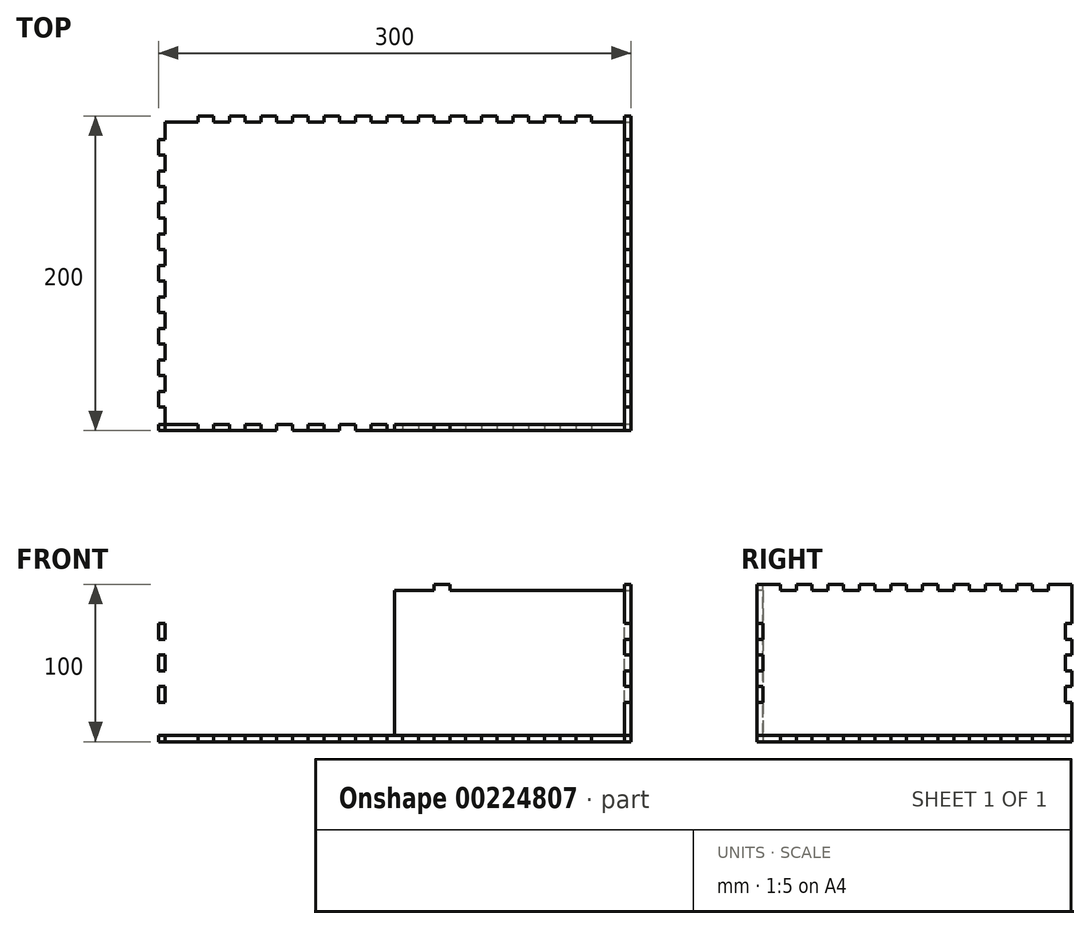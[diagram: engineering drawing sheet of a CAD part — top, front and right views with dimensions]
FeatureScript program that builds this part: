
annotation { "Feature Type Name" : "Feature", "Feature Type Description" : "" }
export const myFeature = defineFeature(function(context is Context, id is Id, definition is map)
    precondition{}
    {
        {
            var Q0;
            Q0=qCreatedBy(makeId("Top.planeOp"),FACE);
            var sketch = newSketch(context, id + "F0", { "sketchPlane" : qUnion([Q0])});
            skLineSegment(sketch, "E0.left", {"start": v(150, -85) * mm, "end": v(150, -75) * mm});
            skLineSegment(sketch, "E0.right", {"start": v(-150, -85) * mm, "end": v(-150, -75) * mm});
            skPoint(sketch, "E0.middle", {"position": v(0, 0) * mm});
            skLineSegment(sketch, "E1", {"start": v(0, 100) * mm, "end": v(0, 96) * mm});
            skPoint(sketch, "E1.endSnap0", {"position": v(0, 100) * mm});
            skLineSegment(sketch, "E2", {"start": v(0, 96) * mm, "end": v(5, 96) * mm});
            skLineSegment(sketch, "E3", {"start": v(5, 96) * mm, "end": v(5, 100) * mm});
            skLineSegment(sketch, "E4.MirrorCS", {"start": v(-5, 96) * mm, "end": v(-5, 100) * mm});
            skLineSegment(sketch, "E5.1.0.0", {"start": v(20, 96) * mm, "end": v(25, 96) * mm});
            skPoint(sketch, "E5.1.0.1", {"position": v(20, 100) * mm});
            skLineSegment(sketch, "E5.1.0.2", {"start": v(25, 96) * mm, "end": v(25, 100) * mm});
            skLineSegment(sketch, "E5.1.0.3", {"start": v(15, 96) * mm, "end": v(15, 100) * mm});
            skLineSegment(sketch, "E5.2.0.0", {"start": v(40, 96) * mm, "end": v(45, 96) * mm});
            skPoint(sketch, "E5.2.0.1", {"position": v(40, 100) * mm});
            skLineSegment(sketch, "E5.2.0.2", {"start": v(45, 96) * mm, "end": v(45, 100) * mm});
            skLineSegment(sketch, "E5.2.0.3", {"start": v(35, 96) * mm, "end": v(35, 100) * mm});
            skLineSegment(sketch, "E5.3.0.0", {"start": v(60, 96) * mm, "end": v(65, 96) * mm});
            skPoint(sketch, "E5.3.0.1", {"position": v(60, 100) * mm});
            skLineSegment(sketch, "E5.3.0.2", {"start": v(65, 96) * mm, "end": v(65, 100) * mm});
            skLineSegment(sketch, "E5.3.0.3", {"start": v(55, 96) * mm, "end": v(55, 100) * mm});
            skLineSegment(sketch, "E5.4.0.0", {"start": v(80, 96) * mm, "end": v(85, 96) * mm});
            skPoint(sketch, "E5.4.0.1", {"position": v(80, 100) * mm});
            skLineSegment(sketch, "E5.4.0.2", {"start": v(85, 96) * mm, "end": v(85, 100) * mm});
            skLineSegment(sketch, "E5.4.0.3", {"start": v(75, 96) * mm, "end": v(75, 100) * mm});
            skLineSegment(sketch, "E5.5.0.0", {"start": v(100, 96) * mm, "end": v(105, 96) * mm});
            skPoint(sketch, "E5.5.0.1", {"position": v(100, 100) * mm});
            skLineSegment(sketch, "E5.5.0.2", {"start": v(105, 96) * mm, "end": v(105, 100) * mm});
            skLineSegment(sketch, "E5.5.0.3", {"start": v(95, 96) * mm, "end": v(95, 100) * mm});
            skLineSegment(sketch, "E5.direction1", {"start": v(-5, 96) * mm, "end": v(15, 96) * mm, "construction": true});
            skLineSegment(sketch, "E6", {"start": v(0, 96) * mm, "end": v(146, 96) * mm});
            skLineSegment(sketch, "E7", {"start": v(-146, 96) * mm, "end": v(146, 96) * mm});
            skLineSegment(sketch, "E8.trimOffspring", {"start": v(5, 100) * mm, "end": v(-5, 100) * mm});
            skLineSegment(sketch, "E9.trimOffspring", {"start": v(25, 100) * mm, "end": v(15, 100) * mm});
            skLineSegment(sketch, "E10.trimOffspring", {"start": v(45, 100) * mm, "end": v(35, 100) * mm});
            skLineSegment(sketch, "E11.trimOffspring", {"start": v(65, 100) * mm, "end": v(55, 100) * mm});
            skLineSegment(sketch, "E12.trimOffspring", {"start": v(85, 100) * mm, "end": v(75, 100) * mm});
            skLineSegment(sketch, "E13.trimOffspring", {"start": v(105, 100) * mm, "end": v(95, 100) * mm});
            skLineSegment(sketch, "E14.trimOffspring", {"start": v(125, 100) * mm, "end": v(115, 100) * mm});
            skLineSegment(sketch, "E15.MirrorCS", {"start": v(-65, 96) * mm, "end": v(-65, 100) * mm});
            skLineSegment(sketch, "E16.MirrorCS", {"start": v(-125, 96) * mm, "end": v(-125, 100) * mm});
            skLineSegment(sketch, "E17.MirrorCS", {"start": v(-105, 96) * mm, "end": v(-105, 100) * mm});
            skLineSegment(sketch, "E18.MirrorCS", {"start": v(-85, 96) * mm, "end": v(-85, 100) * mm});
            skLineSegment(sketch, "E19.MirrorCS", {"start": v(-45, 96) * mm, "end": v(-45, 100) * mm});
            skLineSegment(sketch, "E20.MirrorCS", {"start": v(-15, 96) * mm, "end": v(-15, 100) * mm});
            skLineSegment(sketch, "E21.MirrorCS", {"start": v(-25, 96) * mm, "end": v(-25, 100) * mm});
            skLineSegment(sketch, "E22.MirrorCS", {"start": v(-75, 96) * mm, "end": v(-75, 100) * mm});
            skLineSegment(sketch, "E23.MirrorCS", {"start": v(-65, 100) * mm, "end": v(-55, 100) * mm});
            skLineSegment(sketch, "E24.MirrorCS", {"start": v(-60, 96) * mm, "end": v(-65, 96) * mm});
            skLineSegment(sketch, "E25.MirrorCS", {"start": v(-125, 100) * mm, "end": v(-115, 100) * mm});
            skLineSegment(sketch, "E26.MirrorCS", {"start": v(-95, 96) * mm, "end": v(-95, 100) * mm});
            skLineSegment(sketch, "E27.MirrorCS", {"start": v(-20, 96) * mm, "end": v(-25, 96) * mm});
            skLineSegment(sketch, "E28.MirrorCS", {"start": v(-55, 96) * mm, "end": v(-55, 100) * mm});
            skLineSegment(sketch, "E29.MirrorCS", {"start": v(-105, 100) * mm, "end": v(-95, 100) * mm});
            skLineSegment(sketch, "E30.MirrorCS", {"start": v(-45, 100) * mm, "end": v(-35, 100) * mm});
            skLineSegment(sketch, "E31.MirrorCS", {"start": v(-40, 96) * mm, "end": v(-45, 96) * mm});
            skLineSegment(sketch, "E32.MirrorCS", {"start": v(-35, 96) * mm, "end": v(-35, 100) * mm});
            skLineSegment(sketch, "E33.MirrorCS", {"start": v(-85, 100) * mm, "end": v(-75, 100) * mm});
            skLineSegment(sketch, "E34.MirrorCS", {"start": v(-25, 100) * mm, "end": v(-15, 100) * mm});
            skLineSegment(sketch, "E35.MirrorCS", {"start": v(-100, 96) * mm, "end": v(-105, 96) * mm});
            skLineSegment(sketch, "E36.MirrorCS", {"start": v(-115, 96) * mm, "end": v(-115, 100) * mm});
            skLineSegment(sketch, "E37.MirrorCS", {"start": v(-80, 96) * mm, "end": v(-85, 96) * mm});
            skLineSegment(sketch, "E38.MirrorCS", {"start": v(-120, 96) * mm, "end": v(-125, 96) * mm});
            skPoint(sketch, "E39.MirrorP", {"position": v(-80, 100) * mm});
            skPoint(sketch, "E40.MirrorP", {"position": v(-60, 100) * mm});
            skPoint(sketch, "E41.MirrorP", {"position": v(-100, 100) * mm});
            skPoint(sketch, "E42.MirrorP", {"position": v(-120, 100) * mm});
            skPoint(sketch, "E43.MirrorP", {"position": v(-20, 100) * mm});
            skPoint(sketch, "E44.MirrorP", {"position": v(-40, 100) * mm});
            skLineSegment(sketch, "E45.trimOffspring", {"start": v(-15, 100) * mm, "end": v(-25, 100) * mm});
            skLineSegment(sketch, "E46.trimOffspring", {"start": v(-35, 100) * mm, "end": v(-45, 100) * mm});
            skLineSegment(sketch, "E47.trimOffspring", {"start": v(-55, 100) * mm, "end": v(-65, 100) * mm});
            skLineSegment(sketch, "E48.trimOffspring", {"start": v(-75, 100) * mm, "end": v(-85, 100) * mm});
            skLineSegment(sketch, "E49.trimOffspring", {"start": v(-95, 100) * mm, "end": v(-105, 100) * mm});
            skLineSegment(sketch, "E50.trimOffspring", {"start": v(-115, 100) * mm, "end": v(-120, 100) * mm});
            skLineSegment(sketch, "E51.MirrorCS", {"start": v(-105, -96) * mm, "end": v(-105, -100) * mm});
            skLineSegment(sketch, "E52.MirrorCS", {"start": v(-115, -96) * mm, "end": v(-115, -100) * mm});
            skLineSegment(sketch, "E53.MirrorCS", {"start": v(-65, -96) * mm, "end": v(-65, -100) * mm});
            skLineSegment(sketch, "E54.MirrorCS", {"start": v(-55, -96) * mm, "end": v(-55, -100) * mm});
            skLineSegment(sketch, "E55.MirrorCS", {"start": v(-75, -96) * mm, "end": v(-75, -100) * mm});
            skLineSegment(sketch, "E56.MirrorCS", {"start": v(-25, -96) * mm, "end": v(-25, -100) * mm});
            skLineSegment(sketch, "E57.MirrorCS", {"start": v(-15, -96) * mm, "end": v(-15, -100) * mm});
            skLineSegment(sketch, "E58.MirrorCS", {"start": v(-45, -96) * mm, "end": v(-45, -100) * mm});
            skLineSegment(sketch, "E59.MirrorCS", {"start": v(-35, -96) * mm, "end": v(-35, -100) * mm});
            skLineSegment(sketch, "E60.MirrorCS", {"start": v(-95, -96) * mm, "end": v(-95, -100) * mm});
            skLineSegment(sketch, "E61.MirrorCS", {"start": v(-85, -96) * mm, "end": v(-85, -100) * mm});
            skLineSegment(sketch, "E62.MirrorCS", {"start": v(-125, -100) * mm, "end": v(-115, -100) * mm});
            skLineSegment(sketch, "E63.MirrorCS", {"start": v(-120, -96) * mm, "end": v(-125, -96) * mm});
            skLineSegment(sketch, "E64.MirrorCS", {"start": v(85, -96) * mm, "end": v(85, -100) * mm});
            skLineSegment(sketch, "E65.MirrorCS", {"start": v(125, -96) * mm, "end": v(125, -100) * mm});
            skLineSegment(sketch, "E66.MirrorCS", {"start": v(-115, -100) * mm, "end": v(-120, -100) * mm});
            skLineSegment(sketch, "E67.MirrorCS", {"start": v(-125, -96) * mm, "end": v(-125, -100) * mm});
            skLineSegment(sketch, "E68.MirrorCS", {"start": v(5, -100) * mm, "end": v(-5, -100) * mm});
            skLineSegment(sketch, "E69.MirrorCS", {"start": v(55, -96) * mm, "end": v(55, -100) * mm});
            skLineSegment(sketch, "E70.MirrorCS", {"start": v(-95, -100) * mm, "end": v(-105, -100) * mm});
            skLineSegment(sketch, "E71.MirrorCS", {"start": v(45, -96) * mm, "end": v(45, -100) * mm});
            skLineSegment(sketch, "E72.MirrorCS", {"start": v(15, -96) * mm, "end": v(15, -100) * mm});
            skLineSegment(sketch, "E73.MirrorCS", {"start": v(25, -96) * mm, "end": v(25, -100) * mm});
            skLineSegment(sketch, "E74.MirrorCS", {"start": v(-5, -96) * mm, "end": v(-5, -100) * mm});
            skLineSegment(sketch, "E75.MirrorCS", {"start": v(5, -96) * mm, "end": v(5, -100) * mm});
            skLineSegment(sketch, "E76.MirrorCS", {"start": v(0, -96) * mm, "end": v(5, -96) * mm});
            skLineSegment(sketch, "E77.MirrorCS", {"start": v(0, -100) * mm, "end": v(0, -96) * mm});
            skLineSegment(sketch, "E78.MirrorCS", {"start": v(65, -96) * mm, "end": v(65, -100) * mm});
            skLineSegment(sketch, "E79.MirrorCS", {"start": v(35, -96) * mm, "end": v(35, -100) * mm});
            skLineSegment(sketch, "E80.MirrorCS", {"start": v(95, -96) * mm, "end": v(95, -100) * mm});
            skLineSegment(sketch, "E81.MirrorCS", {"start": v(-55, -100) * mm, "end": v(-65, -100) * mm});
            skLineSegment(sketch, "E82.MirrorCS", {"start": v(105, -96) * mm, "end": v(105, -100) * mm});
            skLineSegment(sketch, "E83.MirrorCS", {"start": v(-35, -100) * mm, "end": v(-45, -100) * mm});
            skLineSegment(sketch, "E84.MirrorCS", {"start": v(-85, -100) * mm, "end": v(-75, -100) * mm});
            skLineSegment(sketch, "E85.MirrorCS", {"start": v(-15, -100) * mm, "end": v(-25, -100) * mm});
            skLineSegment(sketch, "E86.MirrorCS", {"start": v(75, -96) * mm, "end": v(75, -100) * mm});
            skLineSegment(sketch, "E87.MirrorCS", {"start": v(115, -96) * mm, "end": v(115, -100) * mm});
            skLineSegment(sketch, "E88.MirrorCS", {"start": v(45, -100) * mm, "end": v(35, -100) * mm});
            skLineSegment(sketch, "E89.MirrorCS", {"start": v(-45, -100) * mm, "end": v(-35, -100) * mm});
            skLineSegment(sketch, "E90.MirrorCS", {"start": v(25, -100) * mm, "end": v(15, -100) * mm});
            skLineSegment(sketch, "E91.MirrorCS", {"start": v(-60, -96) * mm, "end": v(-65, -96) * mm});
            skLineSegment(sketch, "E92.MirrorCS", {"start": v(-80, -96) * mm, "end": v(-85, -96) * mm});
            skLineSegment(sketch, "E93.MirrorCS", {"start": v(80, -96) * mm, "end": v(85, -96) * mm});
            skLineSegment(sketch, "E94.MirrorCS", {"start": v(120, -96) * mm, "end": v(125, -96) * mm});
            skLineSegment(sketch, "E95.MirrorCS", {"start": v(-105, -100) * mm, "end": v(-95, -100) * mm});
            skLineSegment(sketch, "E96.MirrorCS", {"start": v(-65, -100) * mm, "end": v(-55, -100) * mm});
            skLineSegment(sketch, "E97.MirrorCS", {"start": v(40, -96) * mm, "end": v(45, -96) * mm});
            skLineSegment(sketch, "E98.MirrorCS", {"start": v(20, -96) * mm, "end": v(25, -96) * mm});
            skLineSegment(sketch, "E99.MirrorCS", {"start": v(60, -96) * mm, "end": v(65, -96) * mm});
            skLineSegment(sketch, "E100.MirrorCS", {"start": v(125, -100) * mm, "end": v(115, -100) * mm});
            skLineSegment(sketch, "E101.MirrorCS", {"start": v(-75, -100) * mm, "end": v(-85, -100) * mm});
            skLineSegment(sketch, "E102.MirrorCS", {"start": v(-100, -96) * mm, "end": v(-105, -96) * mm});
            skLineSegment(sketch, "E103.MirrorCS", {"start": v(105, -100) * mm, "end": v(95, -100) * mm});
            skLineSegment(sketch, "E104.MirrorCS", {"start": v(-20, -96) * mm, "end": v(-25, -96) * mm});
            skLineSegment(sketch, "E105.MirrorCS", {"start": v(-25, -100) * mm, "end": v(-15, -100) * mm});
            skLineSegment(sketch, "E106.MirrorCS", {"start": v(85, -100) * mm, "end": v(75, -100) * mm});
            skLineSegment(sketch, "E107.MirrorCS", {"start": v(100, -96) * mm, "end": v(105, -96) * mm});
            skLineSegment(sketch, "E108.MirrorCS", {"start": v(140, -96) * mm, "end": v(145, -96) * mm});
            skLineSegment(sketch, "E109.MirrorCS", {"start": v(65, -100) * mm, "end": v(55, -100) * mm});
            skLineSegment(sketch, "E110.MirrorCS", {"start": v(-40, -96) * mm, "end": v(-45, -96) * mm});
            skPoint(sketch, "E111.MirrorP", {"position": v(80, -100) * mm});
            skPoint(sketch, "E112.MirrorP", {"position": v(-20, -100) * mm});
            skPoint(sketch, "E113.MirrorP", {"position": v(60, -100) * mm});
            skPoint(sketch, "E114.MirrorP", {"position": v(-120, -100) * mm});
            skPoint(sketch, "E115.MirrorP", {"position": v(-100, -100) * mm});
            skLineSegment(sketch, "E116.MirrorCS", {"start": v(-5, -96) * mm, "end": v(15, -96) * mm, "construction": true});
            skPoint(sketch, "E117.MirrorP", {"position": v(40, -100) * mm});
            skPoint(sketch, "E118.MirrorP", {"position": v(20, -100) * mm});
            skPoint(sketch, "E119.MirrorP", {"position": v(0, -100) * mm});
            skPoint(sketch, "E120.MirrorP", {"position": v(-60, -100) * mm});
            skPoint(sketch, "E121.MirrorP", {"position": v(120, -100) * mm});
            skPoint(sketch, "E122.MirrorP", {"position": v(-80, -100) * mm});
            skPoint(sketch, "E123.MirrorP", {"position": v(100, -100) * mm});
            skPoint(sketch, "E124.MirrorP", {"position": v(-40, -100) * mm});
            skLineSegment(sketch, "E125", {"start": v(-146, -96) * mm, "end": v(146, -96) * mm});
            skPoint(sketch, "E126.orphan", {"position": v(-150, -100) * mm});
            skLineSegment(sketch, "E127.trimOffspring", {"start": v(-115, -100) * mm, "end": v(-125, -100) * mm});
            skLineSegment(sketch, "E128", {"start": v(150, 0) * mm, "end": v(146, 0) * mm});
            skPoint(sketch, "E128.endSnap0", {"position": v(150, 0) * mm});
            skLineSegment(sketch, "E129", {"start": v(150, -5) * mm, "end": v(146, -5) * mm});
            skLineSegment(sketch, "E130.MirrorCS", {"start": v(150, 5) * mm, "end": v(146, 5) * mm});
            skLineSegment(sketch, "E131", {"start": v(146, 5) * mm, "end": v(146, -96) * mm});
            skLineSegment(sketch, "E132", {"start": v(146, -96) * mm, "end": v(146, 96) * mm});
            skPoint(sketch, "E133.0.1.0", {"position": v(150, -20) * mm});
            skLineSegment(sketch, "E133.0.1.1", {"start": v(150, -25) * mm, "end": v(146, -25) * mm});
            skLineSegment(sketch, "E133.0.1.3", {"start": v(150, -15) * mm, "end": v(146, -15) * mm});
            skPoint(sketch, "E133.0.2.0", {"position": v(150, -40) * mm});
            skLineSegment(sketch, "E133.0.2.1", {"start": v(150, -45) * mm, "end": v(146, -45) * mm});
            skLineSegment(sketch, "E133.0.2.3", {"start": v(150, -35) * mm, "end": v(146, -35) * mm});
            skPoint(sketch, "E133.0.3.0", {"position": v(150, -60) * mm});
            skLineSegment(sketch, "E133.0.3.1", {"start": v(150, -65) * mm, "end": v(146, -65) * mm});
            skLineSegment(sketch, "E133.0.3.3", {"start": v(150, -55) * mm, "end": v(146, -55) * mm});
            skPoint(sketch, "E133.0.4.0", {"position": v(150, -80) * mm});
            skLineSegment(sketch, "E133.0.4.1", {"start": v(150, -85) * mm, "end": v(146, -85) * mm});
            skLineSegment(sketch, "E133.0.4.2", {"start": v(150, -80) * mm, "end": v(146, -80) * mm});
            skLineSegment(sketch, "E133.0.4.3", {"start": v(150, -75) * mm, "end": v(146, -75) * mm});
            skLineSegment(sketch, "E133.direction1", {"start": v(146, -5) * mm, "end": v(171, -5) * mm, "construction": true});
            skLineSegment(sketch, "E133.direction2", {"start": v(146, -5) * mm, "end": v(146, -25) * mm, "construction": true});
            skLineSegment(sketch, "E134.trimOffspring", {"start": v(150, -5) * mm, "end": v(150, 5) * mm});
            skLineSegment(sketch, "E135.trimOffspring", {"start": v(150, -25) * mm, "end": v(150, -15) * mm});
            skLineSegment(sketch, "E136.trimOffspring", {"start": v(150, -45) * mm, "end": v(150, -35) * mm});
            skLineSegment(sketch, "E137.trimOffspring", {"start": v(150, -65) * mm, "end": v(150, -55) * mm});
            skLineSegment(sketch, "E138.MirrorCS", {"start": v(150, 25) * mm, "end": v(146, 25) * mm});
            skLineSegment(sketch, "E139.MirrorCS", {"start": v(150, 65) * mm, "end": v(150, 55) * mm});
            skLineSegment(sketch, "E140.MirrorCS", {"start": v(150, 45) * mm, "end": v(150, 35) * mm});
            skLineSegment(sketch, "E141.MirrorCS", {"start": v(150, 55) * mm, "end": v(146, 55) * mm});
            skLineSegment(sketch, "E142.MirrorCS", {"start": v(150, 35) * mm, "end": v(146, 35) * mm});
            skLineSegment(sketch, "E143.MirrorCS", {"start": v(150, 45) * mm, "end": v(146, 45) * mm});
            skLineSegment(sketch, "E144.MirrorCS", {"start": v(150, 75) * mm, "end": v(146, 75) * mm});
            skLineSegment(sketch, "E145.MirrorCS", {"start": v(150, 65) * mm, "end": v(146, 65) * mm});
            skLineSegment(sketch, "E146.MirrorCS", {"start": v(150, 15) * mm, "end": v(146, 15) * mm});
            skLineSegment(sketch, "E147.MirrorCS", {"start": v(150, 85) * mm, "end": v(146, 85) * mm});
            skPoint(sketch, "E148.MirrorP", {"position": v(150, 60) * mm});
            skPoint(sketch, "E149.MirrorP", {"position": v(150, 40) * mm});
            skLineSegment(sketch, "E150.MirrorCS", {"start": v(150, 25) * mm, "end": v(150, 15) * mm});
            skLineSegment(sketch, "E151.MirrorCS", {"start": v(150, 85) * mm, "end": v(150, 75) * mm});
            skPoint(sketch, "E152.MirrorP", {"position": v(150, 80) * mm});
            skPoint(sketch, "E153.MirrorP", {"position": v(150, 20) * mm});
            skLineSegment(sketch, "E154.trimOffspring", {"start": v(150, 75) * mm, "end": v(150, 85) * mm});
            skLineSegment(sketch, "E155.trimOffspring", {"start": v(150, 55) * mm, "end": v(150, 65) * mm});
            skLineSegment(sketch, "E156.trimOffspring", {"start": v(150, 35) * mm, "end": v(150, 45) * mm});
            skLineSegment(sketch, "E157.trimOffspring", {"start": v(150, 15) * mm, "end": v(150, 25) * mm});
            skPoint(sketch, "E158.MirrorCS.end.orphan", {"position": v(146, 20) * mm});
            skPoint(sketch, "E159.MirrorCS.end.orphan", {"position": v(146, 40) * mm});
            skPoint(sketch, "E160.MirrorCS.end.orphan", {"position": v(146, 60) * mm});
            skPoint(sketch, "E161.MirrorCS.end.orphan", {"position": v(146, 80) * mm});
            skPoint(sketch, "E133.0.3.2.end.orphan", {"position": v(146, -60) * mm});
            skPoint(sketch, "E133.0.3.2.start.orphan", {"position": v(150, -60) * mm});
            skPoint(sketch, "E133.0.2.2.end.orphan", {"position": v(146, -40) * mm});
            skPoint(sketch, "E133.0.2.2.start.orphan", {"position": v(150, -40) * mm});
            skPoint(sketch, "E133.0.1.2.end.orphan", {"position": v(146, -20) * mm});
            skPoint(sketch, "E133.0.1.2.start.orphan", {"position": v(150, -20) * mm});
            skLineSegment(sketch, "E162.MirrorCS", {"start": v(-150, 45) * mm, "end": v(-150, 35) * mm});
            skLineSegment(sketch, "E163.MirrorCS", {"start": v(-150, 85) * mm, "end": v(-150, 75) * mm});
            skLineSegment(sketch, "E164.MirrorCS", {"start": v(-150, 25) * mm, "end": v(-150, 15) * mm});
            skLineSegment(sketch, "E165.MirrorCS", {"start": v(-150, 65) * mm, "end": v(-150, 55) * mm});
            skLineSegment(sketch, "E166.MirrorCS", {"start": v(-150, 45) * mm, "end": v(-146, 45) * mm});
            skLineSegment(sketch, "E167.MirrorCS", {"start": v(-150, 75) * mm, "end": v(-146, 75) * mm});
            skLineSegment(sketch, "E168.MirrorCS", {"start": v(-150, -80) * mm, "end": v(-146, -80) * mm});
            skLineSegment(sketch, "E169.MirrorCS", {"start": v(-150, 85) * mm, "end": v(-146, 85) * mm});
            skLineSegment(sketch, "E170.MirrorCS", {"start": v(-150, 75) * mm, "end": v(-150, 85) * mm});
            skLineSegment(sketch, "E171.MirrorCS", {"start": v(-150, 0) * mm, "end": v(-146, 0) * mm});
            skLineSegment(sketch, "E172.MirrorCS", {"start": v(-150, 35) * mm, "end": v(-150, 45) * mm});
            skLineSegment(sketch, "E173.MirrorCS", {"start": v(-150, 35) * mm, "end": v(-146, 35) * mm});
            skLineSegment(sketch, "E174.MirrorCS", {"start": v(-150, 55) * mm, "end": v(-146, 55) * mm});
            skLineSegment(sketch, "E175.MirrorCS", {"start": v(-150, -5) * mm, "end": v(-146, -5) * mm});
            skLineSegment(sketch, "E176.MirrorCS", {"start": v(-150, 55) * mm, "end": v(-150, 65) * mm});
            skLineSegment(sketch, "E177.MirrorCS", {"start": v(-150, 15) * mm, "end": v(-150, 25) * mm});
            skLineSegment(sketch, "E178.MirrorCS", {"start": v(-150, 65) * mm, "end": v(-146, 65) * mm});
            skLineSegment(sketch, "E179.MirrorCS", {"start": v(-150, 25) * mm, "end": v(-146, 25) * mm});
            skLineSegment(sketch, "E180.MirrorCS", {"start": v(-150, 15) * mm, "end": v(-146, 15) * mm});
            skLineSegment(sketch, "E181.MirrorCS", {"start": v(-150, -15) * mm, "end": v(-146, -15) * mm});
            skLineSegment(sketch, "E182.MirrorCS", {"start": v(-150, -35) * mm, "end": v(-146, -35) * mm});
            skLineSegment(sketch, "E183.MirrorCS", {"start": v(-150, -65) * mm, "end": v(-146, -65) * mm});
            skLineSegment(sketch, "E184.MirrorCS", {"start": v(-150, -55) * mm, "end": v(-146, -55) * mm});
            skLineSegment(sketch, "E185.MirrorCS", {"start": v(-146, -5) * mm, "end": v(-146, -25) * mm, "construction": true});
            skLineSegment(sketch, "E186.MirrorCS", {"start": v(-150, -5) * mm, "end": v(-150, 5) * mm});
            skLineSegment(sketch, "E187.MirrorCS", {"start": v(-150, 5) * mm, "end": v(-146, 5) * mm});
            skLineSegment(sketch, "E188.MirrorCS", {"start": v(-150, -45) * mm, "end": v(-150, -35) * mm});
            skLineSegment(sketch, "E189.MirrorCS", {"start": v(-150, -75) * mm, "end": v(-146, -75) * mm});
            skLineSegment(sketch, "E190.MirrorCS", {"start": v(-150, -25) * mm, "end": v(-150, -15) * mm});
            skLineSegment(sketch, "E191.MirrorCS", {"start": v(-150, -45) * mm, "end": v(-146, -45) * mm});
            skLineSegment(sketch, "E192.MirrorCS", {"start": v(-150, -85) * mm, "end": v(-146, -85) * mm});
            skLineSegment(sketch, "E193.MirrorCS", {"start": v(-150, -65) * mm, "end": v(-150, -55) * mm});
            skLineSegment(sketch, "E194.MirrorCS", {"start": v(-150, -25) * mm, "end": v(-146, -25) * mm});
            skPoint(sketch, "E195.MirrorP", {"position": v(-150, -20) * mm});
            skPoint(sketch, "E196.MirrorP", {"position": v(-150, 80) * mm});
            skPoint(sketch, "E197.MirrorP", {"position": v(-150, -40) * mm});
            skPoint(sketch, "E198.MirrorP", {"position": v(-150, 40) * mm});
            skPoint(sketch, "E199.MirrorP", {"position": v(-150, 60) * mm});
            skPoint(sketch, "E200.MirrorP", {"position": v(-150, 20) * mm});
            skPoint(sketch, "E201.MirrorP", {"position": v(-150, -60) * mm});
            skPoint(sketch, "E202.MirrorP", {"position": v(-146, 80) * mm});
            skPoint(sketch, "E203.MirrorP", {"position": v(-150, -80) * mm});
            skPoint(sketch, "E204.MirrorP", {"position": v(-146, -40) * mm});
            skPoint(sketch, "E205.MirrorP", {"position": v(-150, 0) * mm});
            skPoint(sketch, "E206.MirrorP", {"position": v(-146, -60) * mm});
            skPoint(sketch, "E207.MirrorP", {"position": v(-150, -96) * mm});
            skPoint(sketch, "E208.MirrorP", {"position": v(-146, -20) * mm});
            skPoint(sketch, "E209.MirrorP", {"position": v(-146, 60) * mm});
            skPoint(sketch, "E210.MirrorP", {"position": v(-146, 40) * mm});
            skPoint(sketch, "E211.MirrorP", {"position": v(-146, 20) * mm});
            skLineSegment(sketch, "E212", {"start": v(-146, 96) * mm, "end": v(-146, -96) * mm});
            skLineSegment(sketch, "E213.0.6.0", {"start": v(120, 96) * mm, "end": v(125, 96) * mm});
            skPoint(sketch, "E213.3.6.0", {"position": v(120, 100) * mm});
            skLineSegment(sketch, "E213.4.6.0", {"start": v(125, 96) * mm, "end": v(125, 100) * mm});
            skLineSegment(sketch, "E213.7.6.0", {"start": v(115, 96) * mm, "end": v(115, 100) * mm});
            skLineSegment(sketch, "E213.10.6.0", {"start": v(120, 100) * mm, "end": v(120, 96) * mm});
            skSolve(sketch);
        }
        {
            var Q0;
            Q0 = qSketchRegion(id + "F0", true);
            extrude(context, id + "F1", {"entities" : qUnion([Q0]), "depth" : 4 * mm});
        }
        {
            var Q0;
            Q0=makeQuery(id+"F1.opExtrude","SWEPT_FACE",FACE,{"disambiguationData":[OSD([sQuery(id+"F0.wireOp",EDGE,"E85.MirrorCS")])]});
            var sketch = newSketch(context, id + "F2", { "sketchPlane" : qUnion([Q0])});
            skLineSegment(sketch, "E214.0", {"start": v(146, 4) * mm, "end": v(146, 0) * mm});
            skLineSegment(sketch, "E214.1", {"start": v(55, 4) * mm, "end": v(55, 0) * mm});
            skLineSegment(sketch, "E214.2", {"start": v(-115, 0) * mm, "end": v(-105, 0) * mm});
            skLineSegment(sketch, "E214.4", {"start": v(65, 4) * mm, "end": v(65, 0) * mm});
            skLineSegment(sketch, "E214.5", {"start": v(85, 4) * mm, "end": v(75, 4) * mm});
            skLineSegment(sketch, "E214.6", {"start": v(-75, 4) * mm, "end": v(-75, 0) * mm});
            skLineSegment(sketch, "E214.7", {"start": v(-35, 0) * mm, "end": v(-45, 0) * mm});
            skLineSegment(sketch, "E214.8", {"start": v(-95, 0) * mm, "end": v(-85, 0) * mm});
            skLineSegment(sketch, "E214.10", {"start": v(105, 4) * mm, "end": v(105, 0) * mm});
            skLineSegment(sketch, "E214.11", {"start": v(-95, 4) * mm, "end": v(-85, 4) * mm});
            skLineSegment(sketch, "E214.12", {"start": v(85, 4) * mm, "end": v(85, 0) * mm});
            skLineSegment(sketch, "E214.13", {"start": v(-95, 4) * mm, "end": v(-105, 4) * mm});
            skLineSegment(sketch, "E214.15", {"start": v(125, 0) * mm, "end": v(115, 0) * mm});
            skLineSegment(sketch, "E214.16", {"start": v(125, 4) * mm, "end": v(125, 0) * mm});
            skLineSegment(sketch, "E214.18", {"start": v(45, 0) * mm, "end": v(55, 0) * mm});
            skLineSegment(sketch, "E214.19", {"start": v(125, 4) * mm, "end": v(125, 0) * mm});
            skLineSegment(sketch, "E214.20", {"start": v(65, 4) * mm, "end": v(75, 4) * mm});
            skLineSegment(sketch, "E214.21", {"start": v(85, 0) * mm, "end": v(75, 0) * mm});
            skLineSegment(sketch, "E214.22", {"start": v(65, 0) * mm, "end": v(55, 0) * mm});
            skLineSegment(sketch, "E214.23", {"start": v(45, 4) * mm, "end": v(45, 0) * mm});
            skLineSegment(sketch, "E214.24", {"start": v(-35, 4) * mm, "end": v(-35, 0) * mm});
            skLineSegment(sketch, "E214.25", {"start": v(35, 4) * mm, "end": v(35, 0) * mm});
            skLineSegment(sketch, "E214.26", {"start": v(105, 0) * mm, "end": v(95, 0) * mm});
            skLineSegment(sketch, "E214.30", {"start": v(-55, 4) * mm, "end": v(-55, 0) * mm});
            skLineSegment(sketch, "E214.31", {"start": v(65, 0) * mm, "end": v(75, 0) * mm});
            skLineSegment(sketch, "E214.32", {"start": v(25, 4) * mm, "end": v(35, 4) * mm});
            skLineSegment(sketch, "E214.35", {"start": v(65, 4) * mm, "end": v(55, 4) * mm});
            skLineSegment(sketch, "E214.36", {"start": v(5, 0) * mm, "end": v(15, 0) * mm});
            skLineSegment(sketch, "E214.39", {"start": v(-15, 4) * mm, "end": v(-5, 4) * mm});
            skLineSegment(sketch, "E214.40", {"start": v(-115, 4) * mm, "end": v(-125, 4) * mm});
            skLineSegment(sketch, "E214.41", {"start": v(45, 4) * mm, "end": v(35, 4) * mm});
            skLineSegment(sketch, "E214.45", {"start": v(-45, 4) * mm, "end": v(-45, 0) * mm});
            skLineSegment(sketch, "E214.46", {"start": v(-75, 4) * mm, "end": v(-85, 4) * mm});
            skLineSegment(sketch, "E214.49", {"start": v(-95, 0) * mm, "end": v(-105, 0) * mm});
            skLineSegment(sketch, "E214.50", {"start": v(65, 4) * mm, "end": v(65, 0) * mm});
            skLineSegment(sketch, "E214.51", {"start": v(-75, 4) * mm, "end": v(-75, 0) * mm});
            skLineSegment(sketch, "E214.52", {"start": v(5, 4) * mm, "end": v(15, 4) * mm});
            skLineSegment(sketch, "E214.53", {"start": v(105, 4) * mm, "end": v(95, 4) * mm});
            skLineSegment(sketch, "E214.54", {"start": v(25, 0) * mm, "end": v(35, 0) * mm});
            skLineSegment(sketch, "E214.55", {"start": v(-75, 0) * mm, "end": v(-85, 0) * mm});
            skLineSegment(sketch, "E214.56", {"start": v(55, 4) * mm, "end": v(55, 0) * mm});
            skLineSegment(sketch, "E214.57", {"start": v(-15, 4) * mm, "end": v(-15, 0) * mm});
            skLineSegment(sketch, "E214.59", {"start": v(85, 0) * mm, "end": v(95, 0) * mm});
            skLineSegment(sketch, "E214.60", {"start": v(105, 4) * mm, "end": v(105, 0) * mm});
            skLineSegment(sketch, "E214.61", {"start": v(125, 4) * mm, "end": v(115, 4) * mm});
            skLineSegment(sketch, "E214.62", {"start": v(-35, 4) * mm, "end": v(-35, 0) * mm});
            skLineSegment(sketch, "E214.63", {"start": v(15, 4) * mm, "end": v(15, 0) * mm});
            skLineSegment(sketch, "E214.64", {"start": v(-15, 4) * mm, "end": v(-25, 4) * mm});
            skLineSegment(sketch, "E214.65", {"start": v(-75, 4) * mm, "end": v(-65, 4) * mm});
            skLineSegment(sketch, "E214.66", {"start": v(5, 4) * mm, "end": v(5, 0) * mm});
            skLineSegment(sketch, "E214.67", {"start": v(-35, 0) * mm, "end": v(-25, 0) * mm});
            skLineSegment(sketch, "E214.68", {"start": v(125, 0) * mm, "end": v(146, 0) * mm});
            skLineSegment(sketch, "E214.69", {"start": v(45, 4) * mm, "end": v(55, 4) * mm});
            skLineSegment(sketch, "E214.70", {"start": v(-25, 4) * mm, "end": v(-25, 0) * mm});
            skLineSegment(sketch, "E214.71", {"start": v(-125, 4) * mm, "end": v(-125, 0) * mm});
            skLineSegment(sketch, "E214.72", {"start": v(-55, 0) * mm, "end": v(-65, 0) * mm});
            skLineSegment(sketch, "E214.73", {"start": v(-55, 4) * mm, "end": v(-65, 4) * mm});
            skLineSegment(sketch, "E214.75", {"start": v(95, 4) * mm, "end": v(95, 0) * mm});
            skLineSegment(sketch, "E214.76", {"start": v(-15, 4) * mm, "end": v(-15, 0) * mm});
            skLineSegment(sketch, "E214.77", {"start": v(95, 4) * mm, "end": v(95, 0) * mm});
            skLineSegment(sketch, "E214.78", {"start": v(-115, 4) * mm, "end": v(-105, 4) * mm});
            skLineSegment(sketch, "E214.80", {"start": v(-75, 0) * mm, "end": v(-65, 0) * mm});
            skLineSegment(sketch, "E214.81", {"start": v(-15, 0) * mm, "end": v(-25, 0) * mm});
            skLineSegment(sketch, "E214.82", {"start": v(45, 4) * mm, "end": v(45, 0) * mm});
            skLineSegment(sketch, "E214.83", {"start": v(-35, 4) * mm, "end": v(-45, 4) * mm});
            skLineSegment(sketch, "E214.84", {"start": v(-105, 4) * mm, "end": v(-105, 0) * mm});
            skLineSegment(sketch, "E214.85", {"start": v(75, 4) * mm, "end": v(75, 0) * mm});
            skLineSegment(sketch, "E214.86", {"start": v(85, 4) * mm, "end": v(95, 4) * mm});
            skLineSegment(sketch, "E214.88", {"start": v(35, 4) * mm, "end": v(35, 0) * mm});
            skLineSegment(sketch, "E214.89", {"start": v(-25, 4) * mm, "end": v(-25, 0) * mm});
            skLineSegment(sketch, "E214.90", {"start": v(25, 4) * mm, "end": v(15, 4) * mm});
            skLineSegment(sketch, "E214.91", {"start": v(-5, 4) * mm, "end": v(-5, 0) * mm});
            skLineSegment(sketch, "E214.92", {"start": v(-15, 0) * mm, "end": v(-5, 0) * mm});
            skLineSegment(sketch, "E214.93", {"start": v(-115, 0) * mm, "end": v(-125, 0) * mm});
            skLineSegment(sketch, "E214.94", {"start": v(45, 0) * mm, "end": v(35, 0) * mm});
            skLineSegment(sketch, "E214.95", {"start": v(85, 4) * mm, "end": v(85, 0) * mm});
            skLineSegment(sketch, "E214.96", {"start": v(5, 4) * mm, "end": v(5, 0) * mm});
            skLineSegment(sketch, "E214.98", {"start": v(-35, 4) * mm, "end": v(-25, 4) * mm});
            skLineSegment(sketch, "E214.99", {"start": v(125, 4) * mm, "end": v(146, 4) * mm});
            skLineSegment(sketch, "E214.100", {"start": v(-85, 4) * mm, "end": v(-85, 0) * mm});
            skLineSegment(sketch, "E214.101", {"start": v(-65, 4) * mm, "end": v(-65, 0) * mm});
            skLineSegment(sketch, "E214.102", {"start": v(105, 4) * mm, "end": v(115, 4) * mm});
            skLineSegment(sketch, "E214.103", {"start": v(5, 4) * mm, "end": v(-5, 4) * mm});
            skLineSegment(sketch, "E214.104", {"start": v(-55, 4) * mm, "end": v(-45, 4) * mm});
            skLineSegment(sketch, "E214.105", {"start": v(-95, 4) * mm, "end": v(-95, 0) * mm});
            skLineSegment(sketch, "E214.106", {"start": v(-115, 4) * mm, "end": v(-115, 0) * mm});
            skLineSegment(sketch, "E214.107", {"start": v(25, 4) * mm, "end": v(25, 0) * mm});
            skLineSegment(sketch, "E214.108", {"start": v(115, 4) * mm, "end": v(115, 0) * mm});
            skLineSegment(sketch, "E214.109", {"start": v(-55, 0) * mm, "end": v(-45, 0) * mm});
            skLineSegment(sketch, "E214.110", {"start": v(105, 0) * mm, "end": v(115, 0) * mm});
            skLineSegment(sketch, "E214.111", {"start": v(5, 0) * mm, "end": v(-5, 0) * mm});
            skLineSegment(sketch, "E214.112", {"start": v(25, 4) * mm, "end": v(25, 0) * mm});
            skLineSegment(sketch, "E214.113", {"start": v(115, 4) * mm, "end": v(115, 0) * mm});
            skLineSegment(sketch, "E214.114", {"start": v(25, 0) * mm, "end": v(15, 0) * mm});
            skLineSegment(sketch, "E214.120", {"start": v(-105, 4) * mm, "end": v(-105, 0) * mm});
            skLineSegment(sketch, "E214.122", {"start": v(15, 4) * mm, "end": v(15, 0) * mm});
            skLineSegment(sketch, "E214.124", {"start": v(75, 4) * mm, "end": v(75, 0) * mm});
            skLineSegment(sketch, "E214.129", {"start": v(-125, 4) * mm, "end": v(-125, 0) * mm});
            skLineSegment(sketch, "E214.134", {"start": v(-45, 4) * mm, "end": v(-45, 0) * mm});
            skLineSegment(sketch, "E214.146", {"start": v(146, 4) * mm, "end": v(146, 0) * mm});
            skLineSegment(sketch, "E214.147", {"start": v(-55, 4) * mm, "end": v(-55, 0) * mm});
            skLineSegment(sketch, "E214.149", {"start": v(-65, 4) * mm, "end": v(-65, 0) * mm});
            skLineSegment(sketch, "E214.150", {"start": v(-85, 4) * mm, "end": v(-85, 0) * mm});
            skLineSegment(sketch, "E214.151", {"start": v(-5, 4) * mm, "end": v(-5, 0) * mm});
            skLineSegment(sketch, "E214.158", {"start": v(-115, 4) * mm, "end": v(-115, 0) * mm});
            skLineSegment(sketch, "E214.159", {"start": v(-95, 4) * mm, "end": v(-95, 0) * mm});
            skLineSegment(sketch, "E215.0.0", {"start": v(-146, 0) * mm, "end": v(-125, 0) * mm});
            skLineSegment(sketch, "E215.0.1", {"start": v(-125, 0) * mm, "end": v(-125, 4) * mm});
            skLineSegment(sketch, "E215.0.2", {"start": v(-125, 4) * mm, "end": v(-146, 4) * mm});
            skLineSegment(sketch, "E215.0.3", {"start": v(-146, 4) * mm, "end": v(-146, 0) * mm});
            skSolve(sketch);
        }
        {
            var Q0;
            Q0=makeQuery(id+"F2.imprint","IMPRINT",FACE,{"disambiguationData":[TD([[makeQuery(id+"F2.imprint","IMPRINT",EDGE,{"derivedFrom":sQuery(id+"F2.wireOp",EDGE,"E214.19")}),1.0]])]});
            var Q1;
            Q1=makeQuery(id+"F2.imprint","IMPRINT",FACE,{"disambiguationData":[TD([[makeQuery(id+"F2.imprint","IMPRINT",EDGE,{"derivedFrom":sQuery(id+"F2.wireOp",EDGE,"E215.0.0")}),1.0]])]});
            var Q2;
            Q2=makeQuery(id+"F2.imprint","IMPRINT",FACE,{"disambiguationData":[TD([[makeQuery(id+"F2.imprint","IMPRINT",EDGE,{"derivedFrom":sQuery(id+"F2.wireOp",EDGE,"E214.2")}),1.0]])]});
            var Q3;
            Q3=makeQuery(id+"F2.imprint","IMPRINT",FACE,{"disambiguationData":[TD([[makeQuery(id+"F2.imprint","IMPRINT",EDGE,{"derivedFrom":sQuery(id+"F2.wireOp",EDGE,"E214.8")}),1.0]])]});
            var Q4;
            Q4=makeQuery(id+"F2.imprint","IMPRINT",FACE,{"disambiguationData":[TD([[makeQuery(id+"F2.imprint","IMPRINT",EDGE,{"derivedFrom":sQuery(id+"F2.wireOp",EDGE,"E214.18")}),1.0]])]});
            var Q5;
            Q5=makeQuery(id+"F2.imprint","IMPRINT",FACE,{"disambiguationData":[TD([[makeQuery(id+"F2.imprint","IMPRINT",EDGE,{"derivedFrom":sQuery(id+"F2.wireOp",EDGE,"E214.20")}),-1.0]])]});
            var Q6;
            Q6=makeQuery(id+"F2.imprint","IMPRINT",FACE,{"disambiguationData":[TD([[makeQuery(id+"F2.imprint","IMPRINT",EDGE,{"derivedFrom":sQuery(id+"F2.wireOp",EDGE,"E214.32")}),-1.0]])]});
            var Q7;
            Q7=makeQuery(id+"F2.imprint","IMPRINT",FACE,{"disambiguationData":[TD([[makeQuery(id+"F2.imprint","IMPRINT",EDGE,{"derivedFrom":sQuery(id+"F2.wireOp",EDGE,"E214.36")}),1.0]])]});
            var Q8;
            Q8=makeQuery(id+"F2.imprint","IMPRINT",FACE,{"disambiguationData":[TD([[makeQuery(id+"F2.imprint","IMPRINT",EDGE,{"derivedFrom":sQuery(id+"F2.wireOp",EDGE,"E214.39")}),-1.0]])]});
            var Q9;
            Q9=makeQuery(id+"F2.imprint","IMPRINT",FACE,{"disambiguationData":[TD([[makeQuery(id+"F2.imprint","IMPRINT",EDGE,{"derivedFrom":sQuery(id+"F2.wireOp",EDGE,"E214.51")}),1.0]])]});
            var Q10;
            Q10=makeQuery(id+"F2.imprint","IMPRINT",FACE,{"disambiguationData":[TD([[makeQuery(id+"F2.imprint","IMPRINT",EDGE,{"derivedFrom":sQuery(id+"F2.wireOp",EDGE,"E214.59")}),1.0]])]});
            var Q11;
            Q11=makeQuery(id+"F2.imprint","IMPRINT",FACE,{"disambiguationData":[TD([[makeQuery(id+"F2.imprint","IMPRINT",EDGE,{"derivedFrom":sQuery(id+"F2.wireOp",EDGE,"E214.60")}),1.0]])]});
            var Q12;
            Q12=makeQuery(id+"F2.imprint","IMPRINT",FACE,{"disambiguationData":[TD([[makeQuery(id+"F2.imprint","IMPRINT",EDGE,{"derivedFrom":sQuery(id+"F2.wireOp",EDGE,"E214.62")}),1.0]])]});
            var Q13;
            Q13=makeQuery(id+"F2.imprint","IMPRINT",FACE,{"disambiguationData":[TD([[makeQuery(id+"F2.imprint","IMPRINT",EDGE,{"derivedFrom":sQuery(id+"F2.wireOp",EDGE,"E214.104")}),-1.0]])]});
            var Q14;
            {var subQ0=sQuery(id+"F0.wireOp",EDGE,"E125");Q14=makeQuery(id+"F1.opExtrude","SWEPT_FACE",FACE,{"disambiguationData":[OSD([subQ0]),TDD([makeQuery(id+"F0.imprint","IMPRINT",EDGE,{"disambiguationData":[TD([[makeQuery(id+"F0.imprint","INTERSECT",VERTEX,{"derivedFrom":[sQuery(id+"F0.wireOp",EDGE,"E67.MirrorCS"),subQ0]}),1.0]])],"derivedFrom":subQ0})])]});}
            extrude(context, id + "F3", {"entities" : qUnion([Q0, Q1, Q2, Q3, Q4, Q5, Q6, Q7, Q8, Q9, Q10, Q11, Q12, Q13]), "endBound" : BoundingType.UP_TO_SURFACE, "oppositeDirection" : true, "endBoundEntityFace" : qUnion([Q14]), "depth" : 25 * mm});
        }
        {
            var Q0;
            Q0=makeQuery(id+"F1.opExtrude","SWEPT_FACE",FACE,{"disambiguationData":[OSD([sQuery(id+"F0.wireOp",EDGE,"E134.trimOffspring")])]});
            var sketch = newSketch(context, id + "F4", { "sketchPlane" : qUnion([Q0])});
            skLineSegment(sketch, "E216.0.0", {"start": v(-96, 0) * mm, "end": v(-85, 0) * mm});
            skLineSegment(sketch, "E216.0.1", {"start": v(-85, 0) * mm, "end": v(-85, 4) * mm});
            skLineSegment(sketch, "E216.0.2", {"start": v(-85, 4) * mm, "end": v(-96, 4) * mm});
            skLineSegment(sketch, "E216.1.0", {"start": v(-85, 0) * mm, "end": v(-75, 0) * mm});
            skLineSegment(sketch, "E216.1.1", {"start": v(-75, 0) * mm, "end": v(-75, 4) * mm});
            skLineSegment(sketch, "E216.1.2", {"start": v(-75, 4) * mm, "end": v(-85, 4) * mm});
            skLineSegment(sketch, "E216.1.3", {"start": v(-85, 4) * mm, "end": v(-85, 0) * mm});
            skLineSegment(sketch, "E216.2.0", {"start": v(-75, 0) * mm, "end": v(-65, 0) * mm});
            skLineSegment(sketch, "E216.2.1", {"start": v(-65, 0) * mm, "end": v(-65, 4) * mm});
            skLineSegment(sketch, "E216.2.2", {"start": v(-65, 4) * mm, "end": v(-75, 4) * mm});
            skLineSegment(sketch, "E216.2.3", {"start": v(-75, 4) * mm, "end": v(-75, 0) * mm});
            skLineSegment(sketch, "E216.3.0", {"start": v(-65, 0) * mm, "end": v(-55, 0) * mm});
            skLineSegment(sketch, "E216.3.1", {"start": v(-55, 0) * mm, "end": v(-55, 4) * mm});
            skLineSegment(sketch, "E216.3.2", {"start": v(-55, 4) * mm, "end": v(-65, 4) * mm});
            skLineSegment(sketch, "E216.3.3", {"start": v(-65, 4) * mm, "end": v(-65, 0) * mm});
            skLineSegment(sketch, "E216.4.0", {"start": v(-55, 0) * mm, "end": v(-45, 0) * mm});
            skLineSegment(sketch, "E216.4.1", {"start": v(-45, 0) * mm, "end": v(-45, 4) * mm});
            skLineSegment(sketch, "E216.4.2", {"start": v(-45, 4) * mm, "end": v(-55, 4) * mm});
            skLineSegment(sketch, "E216.4.3", {"start": v(-55, 4) * mm, "end": v(-55, 0) * mm});
            skLineSegment(sketch, "E216.5.0", {"start": v(-45, 0) * mm, "end": v(-35, 0) * mm});
            skLineSegment(sketch, "E216.5.1", {"start": v(-35, 0) * mm, "end": v(-35, 4) * mm});
            skLineSegment(sketch, "E216.5.2", {"start": v(-35, 4) * mm, "end": v(-45, 4) * mm});
            skLineSegment(sketch, "E216.5.3", {"start": v(-45, 4) * mm, "end": v(-45, 0) * mm});
            skLineSegment(sketch, "E216.6.0", {"start": v(-35, 0) * mm, "end": v(-25, 0) * mm});
            skLineSegment(sketch, "E216.6.1", {"start": v(-25, 0) * mm, "end": v(-25, 4) * mm});
            skLineSegment(sketch, "E216.6.2", {"start": v(-25, 4) * mm, "end": v(-35, 4) * mm});
            skLineSegment(sketch, "E216.6.3", {"start": v(-35, 4) * mm, "end": v(-35, 0) * mm});
            skLineSegment(sketch, "E216.7.0", {"start": v(-25, 0) * mm, "end": v(-15, 0) * mm});
            skLineSegment(sketch, "E216.7.1", {"start": v(-15, 0) * mm, "end": v(-15, 4) * mm});
            skLineSegment(sketch, "E216.7.2", {"start": v(-15, 4) * mm, "end": v(-25, 4) * mm});
            skLineSegment(sketch, "E216.7.3", {"start": v(-25, 4) * mm, "end": v(-25, 0) * mm});
            skLineSegment(sketch, "E216.8.0", {"start": v(-15, 0) * mm, "end": v(-5, 0) * mm});
            skLineSegment(sketch, "E216.8.1", {"start": v(-5, 0) * mm, "end": v(-5, 4) * mm});
            skLineSegment(sketch, "E216.8.2", {"start": v(-5, 4) * mm, "end": v(-15, 4) * mm});
            skLineSegment(sketch, "E216.8.3", {"start": v(-15, 4) * mm, "end": v(-15, 0) * mm});
            skLineSegment(sketch, "E216.10.0", {"start": v(5, 0) * mm, "end": v(15, 0) * mm});
            skLineSegment(sketch, "E216.10.1", {"start": v(15, 0) * mm, "end": v(15, 4) * mm});
            skLineSegment(sketch, "E216.10.2", {"start": v(15, 4) * mm, "end": v(5, 4) * mm});
            skLineSegment(sketch, "E216.10.3", {"start": v(5, 4) * mm, "end": v(5, 0) * mm});
            skLineSegment(sketch, "E216.11.0", {"start": v(15, 0) * mm, "end": v(25, 0) * mm});
            skLineSegment(sketch, "E216.11.1", {"start": v(25, 0) * mm, "end": v(25, 4) * mm});
            skLineSegment(sketch, "E216.11.2", {"start": v(25, 4) * mm, "end": v(15, 4) * mm});
            skLineSegment(sketch, "E216.11.3", {"start": v(15, 4) * mm, "end": v(15, 0) * mm});
            skLineSegment(sketch, "E216.12.0", {"start": v(25, 0) * mm, "end": v(35, 0) * mm});
            skLineSegment(sketch, "E216.12.1", {"start": v(35, 0) * mm, "end": v(35, 4) * mm});
            skLineSegment(sketch, "E216.12.2", {"start": v(35, 4) * mm, "end": v(25, 4) * mm});
            skLineSegment(sketch, "E216.12.3", {"start": v(25, 4) * mm, "end": v(25, 0) * mm});
            skLineSegment(sketch, "E216.13.0", {"start": v(35, 0) * mm, "end": v(45, 0) * mm});
            skLineSegment(sketch, "E216.13.1", {"start": v(45, 0) * mm, "end": v(45, 4) * mm});
            skLineSegment(sketch, "E216.13.2", {"start": v(45, 4) * mm, "end": v(35, 4) * mm});
            skLineSegment(sketch, "E216.13.3", {"start": v(35, 4) * mm, "end": v(35, 0) * mm});
            skLineSegment(sketch, "E216.14.0", {"start": v(45, 0) * mm, "end": v(55, 0) * mm});
            skLineSegment(sketch, "E216.14.1", {"start": v(55, 0) * mm, "end": v(55, 4) * mm});
            skLineSegment(sketch, "E216.14.2", {"start": v(55, 4) * mm, "end": v(45, 4) * mm});
            skLineSegment(sketch, "E216.14.3", {"start": v(45, 4) * mm, "end": v(45, 0) * mm});
            skLineSegment(sketch, "E216.15.0", {"start": v(55, 0) * mm, "end": v(65, 0) * mm});
            skLineSegment(sketch, "E216.15.1", {"start": v(65, 0) * mm, "end": v(65, 4) * mm});
            skLineSegment(sketch, "E216.15.2", {"start": v(65, 4) * mm, "end": v(55, 4) * mm});
            skLineSegment(sketch, "E216.15.3", {"start": v(55, 4) * mm, "end": v(55, 0) * mm});
            skLineSegment(sketch, "E216.16.0", {"start": v(65, 0) * mm, "end": v(75, 0) * mm});
            skLineSegment(sketch, "E216.16.1", {"start": v(75, 0) * mm, "end": v(75, 4) * mm});
            skLineSegment(sketch, "E216.16.2", {"start": v(75, 4) * mm, "end": v(65, 4) * mm});
            skLineSegment(sketch, "E216.16.3", {"start": v(65, 4) * mm, "end": v(65, 0) * mm});
            skLineSegment(sketch, "E216.17.0", {"start": v(75, 0) * mm, "end": v(85, 0) * mm});
            skLineSegment(sketch, "E216.17.1", {"start": v(85, 0) * mm, "end": v(85, 4) * mm});
            skLineSegment(sketch, "E216.17.2", {"start": v(85, 4) * mm, "end": v(75, 4) * mm});
            skLineSegment(sketch, "E216.17.3", {"start": v(75, 4) * mm, "end": v(75, 0) * mm});
            skLineSegment(sketch, "E216.18.0", {"start": v(85, 0) * mm, "end": v(96, 0) * mm});
            skLineSegment(sketch, "E216.18.1", {"start": v(96, 0) * mm, "end": v(96, 4) * mm});
            skLineSegment(sketch, "E216.18.2", {"start": v(96, 4) * mm, "end": v(85, 4) * mm});
            skLineSegment(sketch, "E216.18.3", {"start": v(85, 4) * mm, "end": v(85, 0) * mm});
            skLineSegment(sketch, "E217.0.1", {"start": v(-96, 4) * mm, "end": v(-100, 4) * mm});
            skLineSegment(sketch, "E217.0.2", {"start": v(-100, 4) * mm, "end": v(-100, 0) * mm});
            skLineSegment(sketch, "E217.0.3", {"start": v(-100, 0) * mm, "end": v(-96, 0) * mm});
            skLineSegment(sketch, "E218.0.0", {"start": v(96, 0) * mm, "end": v(100, 0) * mm});
            skLineSegment(sketch, "E218.0.1", {"start": v(100, 0) * mm, "end": v(100, 4) * mm});
            skLineSegment(sketch, "E218.0.2", {"start": v(100, 4) * mm, "end": v(96, 4) * mm});
            skLineSegment(sketch, "E218.0.3", {"start": v(96, 4) * mm, "end": v(96, 0) * mm});
            skSolve(sketch);
        }
        {
            var Q0;
            Q0=makeQuery(id+"F4.imprint","IMPRINT",FACE,{"disambiguationData":[TD([[makeQuery(id+"F4.imprint","IMPRINT",EDGE,{"derivedFrom":sQuery(id+"F4.wireOp",EDGE,"E216.0.0")}),1.0]])]});
            var Q1;
            Q1=makeQuery(id+"F4.imprint","IMPRINT",FACE,{"disambiguationData":[TD([[makeQuery(id+"F4.imprint","IMPRINT",EDGE,{"derivedFrom":sQuery(id+"F4.wireOp",EDGE,"E216.18.0")}),1.0]])]});
            var Q2;
            Q2=makeQuery(id+"F4.imprint","IMPRINT",FACE,{"disambiguationData":[TD([[makeQuery(id+"F4.imprint","IMPRINT",EDGE,{"derivedFrom":sQuery(id+"F4.wireOp",EDGE,"E216.2.0")}),1.0]])]});
            var Q3;
            Q3=makeQuery(id+"F4.imprint","IMPRINT",FACE,{"disambiguationData":[TD([[makeQuery(id+"F4.imprint","IMPRINT",EDGE,{"derivedFrom":sQuery(id+"F4.wireOp",EDGE,"E216.4.0")}),1.0]])]});
            var Q4;
            Q4=makeQuery(id+"F4.imprint","IMPRINT",FACE,{"disambiguationData":[TD([[makeQuery(id+"F4.imprint","IMPRINT",EDGE,{"derivedFrom":sQuery(id+"F4.wireOp",EDGE,"E216.6.0")}),1.0]])]});
            var Q5;
            Q5=makeQuery(id+"F4.imprint","IMPRINT",FACE,{"disambiguationData":[TD([[makeQuery(id+"F4.imprint","IMPRINT",EDGE,{"derivedFrom":sQuery(id+"F4.wireOp",EDGE,"E216.8.0")}),1.0]])]});
            var Q6;
            Q6=makeQuery(id+"F4.imprint","IMPRINT",FACE,{"disambiguationData":[TD([[makeQuery(id+"F4.imprint","IMPRINT",EDGE,{"derivedFrom":sQuery(id+"F4.wireOp",EDGE,"E216.10.0")}),1.0]])]});
            var Q7;
            Q7=makeQuery(id+"F4.imprint","IMPRINT",FACE,{"disambiguationData":[TD([[makeQuery(id+"F4.imprint","IMPRINT",EDGE,{"derivedFrom":sQuery(id+"F4.wireOp",EDGE,"E216.12.0")}),1.0]])]});
            var Q8;
            Q8=makeQuery(id+"F4.imprint","IMPRINT",FACE,{"disambiguationData":[TD([[makeQuery(id+"F4.imprint","IMPRINT",EDGE,{"derivedFrom":sQuery(id+"F4.wireOp",EDGE,"E216.14.0")}),1.0]])]});
            var Q9;
            Q9=makeQuery(id+"F4.imprint","IMPRINT",FACE,{"disambiguationData":[TD([[makeQuery(id+"F4.imprint","IMPRINT",EDGE,{"derivedFrom":sQuery(id+"F4.wireOp",EDGE,"E216.16.0")}),1.0]])]});
            var Q10;
            Q10=makeQuery(id+"F4.imprint","IMPRINT",FACE,{"disambiguationData":[TD([[makeQuery(id+"F4.imprint","IMPRINT",EDGE,{"derivedFrom":sQuery(id+"F4.wireOp",EDGE,"E218.0.0")}),1.0]])]});
            var Q11;
            {var subQ0=sQuery(id+"F0.wireOp",EDGE,"E132");Q11=makeQuery(id+"F1.opExtrude","SWEPT_FACE",FACE,{"disambiguationData":[OSD([subQ0]),TDD([makeQuery(id+"F0.imprint","IMPRINT",EDGE,{"disambiguationData":[TD([[makeQuery(id+"F0.imprint","INTERSECT",VERTEX,{"derivedFrom":[sQuery(id+"F0.wireOp",EDGE,"E125"),subQ0]}),-1.0]])],"derivedFrom":subQ0})])]});}
            extrude(context, id + "F5", {"entities" : qUnion([Q0, Q1, Q2, Q3, Q4, Q5, Q6, Q7, Q8, Q9, Q10]), "endBound" : BoundingType.UP_TO_SURFACE, "oppositeDirection" : true, "endBoundEntityFace" : qUnion([Q11]), "depth" : 25 * mm});
        }
        {
            var Q0;
            Q0=makeQuery(id+"F3.opExtrude","CAP_FACE",FACE,{"disambiguationData":[OSD([sQuery(id+"F2.wireOp",EDGE,"E214.32"),sQuery(id+"F2.wireOp",EDGE,"E214.54"),sQuery(id+"F2.wireOp",EDGE,"E214.88"),sQuery(id+"F2.wireOp",EDGE,"E214.112")])],"isStart":true});
            var sketch = newSketch(context, id + "F6", { "sketchPlane" : qUnion([Q0])});
            skLineSegment(sketch, "E219.0.0", {"start": v(-146, 0) * mm, "end": v(-125, 0) * mm});
            skLineSegment(sketch, "E219.0.1", {"start": v(-125, 0) * mm, "end": v(-125, 4) * mm});
            skLineSegment(sketch, "E219.0.2", {"start": v(-125, 4) * mm, "end": v(-146, 4) * mm});
            skLineSegment(sketch, "E219.0.3", {"start": v(-146, 4) * mm, "end": v(-146, 0) * mm});
            skLineSegment(sketch, "E219.1.0", {"start": v(-105, 4) * mm, "end": v(-115, 4) * mm});
            skLineSegment(sketch, "E219.1.1", {"start": v(-115, 4) * mm, "end": v(-115, 0) * mm});
            skLineSegment(sketch, "E219.1.2", {"start": v(-115, 0) * mm, "end": v(-105, 0) * mm});
            skLineSegment(sketch, "E219.1.3", {"start": v(-105, 0) * mm, "end": v(-105, 4) * mm});
            skLineSegment(sketch, "E219.2.0", {"start": v(-125, 0) * mm, "end": v(-115, 0) * mm});
            skLineSegment(sketch, "E219.2.1", {"start": v(-115, 0) * mm, "end": v(-115, 4) * mm});
            skLineSegment(sketch, "E219.2.2", {"start": v(-115, 4) * mm, "end": v(-125, 4) * mm});
            skLineSegment(sketch, "E219.2.3", {"start": v(-125, 4) * mm, "end": v(-125, 0) * mm});
            skLineSegment(sketch, "E219.3.0", {"start": v(-105, 0) * mm, "end": v(-95, 0) * mm});
            skLineSegment(sketch, "E219.3.1", {"start": v(-95, 0) * mm, "end": v(-95, 4) * mm});
            skLineSegment(sketch, "E219.3.2", {"start": v(-95, 4) * mm, "end": v(-105, 4) * mm});
            skLineSegment(sketch, "E219.3.3", {"start": v(-105, 4) * mm, "end": v(-105, 0) * mm});
            skLineSegment(sketch, "E219.4.0", {"start": v(-95, 4) * mm, "end": v(-95, 0) * mm});
            skLineSegment(sketch, "E219.4.1", {"start": v(-95, 0) * mm, "end": v(-85, 0) * mm});
            skLineSegment(sketch, "E219.4.2", {"start": v(-85, 0) * mm, "end": v(-85, 4) * mm});
            skLineSegment(sketch, "E219.4.3", {"start": v(-85, 4) * mm, "end": v(-95, 4) * mm});
            skLineSegment(sketch, "E219.5.0", {"start": v(-85, 0) * mm, "end": v(-75, 0) * mm});
            skLineSegment(sketch, "E219.5.1", {"start": v(-75, 0) * mm, "end": v(-75, 4) * mm});
            skLineSegment(sketch, "E219.5.2", {"start": v(-75, 4) * mm, "end": v(-85, 4) * mm});
            skLineSegment(sketch, "E219.5.3", {"start": v(-85, 4) * mm, "end": v(-85, 0) * mm});
            skLineSegment(sketch, "E219.6.0", {"start": v(-65, 4) * mm, "end": v(-75, 4) * mm});
            skLineSegment(sketch, "E219.6.1", {"start": v(-75, 4) * mm, "end": v(-75, 0) * mm});
            skLineSegment(sketch, "E219.6.2", {"start": v(-75, 0) * mm, "end": v(-65, 0) * mm});
            skLineSegment(sketch, "E219.6.3", {"start": v(-65, 0) * mm, "end": v(-65, 4) * mm});
            skLineSegment(sketch, "E219.7.0", {"start": v(-65, 0) * mm, "end": v(-55, 0) * mm});
            skLineSegment(sketch, "E219.7.1", {"start": v(-55, 0) * mm, "end": v(-55, 4) * mm});
            skLineSegment(sketch, "E219.7.2", {"start": v(-55, 4) * mm, "end": v(-65, 4) * mm});
            skLineSegment(sketch, "E219.7.3", {"start": v(-65, 4) * mm, "end": v(-65, 0) * mm});
            skLineSegment(sketch, "E219.8.0", {"start": v(-45, 0) * mm, "end": v(-45, 4) * mm});
            skLineSegment(sketch, "E219.8.1", {"start": v(-45, 4) * mm, "end": v(-55, 4) * mm});
            skLineSegment(sketch, "E219.8.2", {"start": v(-55, 4) * mm, "end": v(-55, 0) * mm});
            skLineSegment(sketch, "E219.8.3", {"start": v(-55, 0) * mm, "end": v(-45, 0) * mm});
            skLineSegment(sketch, "E219.9.0", {"start": v(-45, 0) * mm, "end": v(-35, 0) * mm});
            skLineSegment(sketch, "E219.9.1", {"start": v(-35, 0) * mm, "end": v(-35, 4) * mm});
            skLineSegment(sketch, "E219.9.2", {"start": v(-35, 4) * mm, "end": v(-45, 4) * mm});
            skLineSegment(sketch, "E219.9.3", {"start": v(-45, 4) * mm, "end": v(-45, 0) * mm});
            skLineSegment(sketch, "E219.10.0", {"start": v(-25, 4) * mm, "end": v(-35, 4) * mm});
            skLineSegment(sketch, "E219.10.1", {"start": v(-35, 4) * mm, "end": v(-35, 0) * mm});
            skLineSegment(sketch, "E219.10.2", {"start": v(-35, 0) * mm, "end": v(-25, 0) * mm});
            skLineSegment(sketch, "E219.10.3", {"start": v(-25, 0) * mm, "end": v(-25, 4) * mm});
            skLineSegment(sketch, "E219.11.0", {"start": v(-25, 0) * mm, "end": v(-15, 0) * mm});
            skLineSegment(sketch, "E219.11.1", {"start": v(-15, 0) * mm, "end": v(-15, 4) * mm});
            skLineSegment(sketch, "E219.11.2", {"start": v(-15, 4) * mm, "end": v(-25, 4) * mm});
            skLineSegment(sketch, "E219.11.3", {"start": v(-25, 4) * mm, "end": v(-25, 0) * mm});
            skLineSegment(sketch, "E219.12.0", {"start": v(-5, 4) * mm, "end": v(-15, 4) * mm});
            skLineSegment(sketch, "E219.12.1", {"start": v(-15, 4) * mm, "end": v(-15, 0) * mm});
            skLineSegment(sketch, "E219.12.2", {"start": v(-15, 0) * mm, "end": v(-5, 0) * mm});
            skLineSegment(sketch, "E219.12.3", {"start": v(-5, 0) * mm, "end": v(-5, 4) * mm});
            skLineSegment(sketch, "E219.13.0", {"start": v(-5, 0) * mm, "end": v(5, 0) * mm});
            skLineSegment(sketch, "E219.13.1", {"start": v(5, 0) * mm, "end": v(5, 4) * mm});
            skLineSegment(sketch, "E219.13.2", {"start": v(5, 4) * mm, "end": v(-5, 4) * mm});
            skLineSegment(sketch, "E219.13.3", {"start": v(-5, 4) * mm, "end": v(-5, 0) * mm});
            skLineSegment(sketch, "E219.14.0", {"start": v(15, 0) * mm, "end": v(25, 0) * mm});
            skLineSegment(sketch, "E219.14.1", {"start": v(25, 0) * mm, "end": v(25, 4) * mm});
            skLineSegment(sketch, "E219.14.2", {"start": v(25, 4) * mm, "end": v(15, 4) * mm});
            skLineSegment(sketch, "E219.14.3", {"start": v(15, 4) * mm, "end": v(15, 0) * mm});
            skLineSegment(sketch, "E219.16.0", {"start": v(15, 4) * mm, "end": v(5, 4) * mm});
            skLineSegment(sketch, "E219.16.1", {"start": v(5, 4) * mm, "end": v(5, 0) * mm});
            skLineSegment(sketch, "E219.16.2", {"start": v(5, 0) * mm, "end": v(15, 0) * mm});
            skLineSegment(sketch, "E219.16.3", {"start": v(15, 0) * mm, "end": v(15, 4) * mm});
            skLineSegment(sketch, "E219.17.0", {"start": v(35, 0) * mm, "end": v(45, 0) * mm});
            skLineSegment(sketch, "E219.17.1", {"start": v(45, 0) * mm, "end": v(45, 4) * mm});
            skLineSegment(sketch, "E219.17.2", {"start": v(45, 4) * mm, "end": v(35, 4) * mm});
            skLineSegment(sketch, "E219.17.3", {"start": v(35, 4) * mm, "end": v(35, 0) * mm});
            skLineSegment(sketch, "E219.18.0", {"start": v(55, 4) * mm, "end": v(45, 4) * mm});
            skLineSegment(sketch, "E219.18.1", {"start": v(45, 4) * mm, "end": v(45, 0) * mm});
            skLineSegment(sketch, "E219.18.2", {"start": v(45, 0) * mm, "end": v(55, 0) * mm});
            skLineSegment(sketch, "E219.18.3", {"start": v(55, 0) * mm, "end": v(55, 4) * mm});
            skLineSegment(sketch, "E219.19.0", {"start": v(55, 0) * mm, "end": v(65, 0) * mm});
            skLineSegment(sketch, "E219.19.1", {"start": v(65, 0) * mm, "end": v(65, 4) * mm});
            skLineSegment(sketch, "E219.19.2", {"start": v(65, 4) * mm, "end": v(55, 4) * mm});
            skLineSegment(sketch, "E219.19.3", {"start": v(55, 4) * mm, "end": v(55, 0) * mm});
            skLineSegment(sketch, "E219.20.0", {"start": v(75, 0) * mm, "end": v(75, 4) * mm});
            skLineSegment(sketch, "E219.20.1", {"start": v(75, 4) * mm, "end": v(65, 4) * mm});
            skLineSegment(sketch, "E219.20.2", {"start": v(65, 4) * mm, "end": v(65, 0) * mm});
            skLineSegment(sketch, "E219.20.3", {"start": v(65, 0) * mm, "end": v(75, 0) * mm});
            skLineSegment(sketch, "E219.21.0", {"start": v(75, 0) * mm, "end": v(85, 0) * mm});
            skLineSegment(sketch, "E219.21.1", {"start": v(85, 0) * mm, "end": v(85, 4) * mm});
            skLineSegment(sketch, "E219.21.2", {"start": v(85, 4) * mm, "end": v(75, 4) * mm});
            skLineSegment(sketch, "E219.21.3", {"start": v(75, 4) * mm, "end": v(75, 0) * mm});
            skLineSegment(sketch, "E219.22.0", {"start": v(95, 4) * mm, "end": v(85, 4) * mm});
            skLineSegment(sketch, "E219.22.1", {"start": v(85, 4) * mm, "end": v(85, 0) * mm});
            skLineSegment(sketch, "E219.22.2", {"start": v(85, 0) * mm, "end": v(95, 0) * mm});
            skLineSegment(sketch, "E219.22.3", {"start": v(95, 0) * mm, "end": v(95, 4) * mm});
            skLineSegment(sketch, "E219.23.0", {"start": v(95, 0) * mm, "end": v(105, 0) * mm});
            skLineSegment(sketch, "E219.23.1", {"start": v(105, 0) * mm, "end": v(105, 4) * mm});
            skLineSegment(sketch, "E219.23.2", {"start": v(105, 4) * mm, "end": v(95, 4) * mm});
            skLineSegment(sketch, "E219.23.3", {"start": v(95, 4) * mm, "end": v(95, 0) * mm});
            skLineSegment(sketch, "E219.24.0", {"start": v(115, 4) * mm, "end": v(105, 4) * mm});
            skLineSegment(sketch, "E219.24.1", {"start": v(105, 4) * mm, "end": v(105, 0) * mm});
            skLineSegment(sketch, "E219.24.2", {"start": v(105, 0) * mm, "end": v(115, 0) * mm});
            skLineSegment(sketch, "E219.24.3", {"start": v(115, 0) * mm, "end": v(115, 4) * mm});
            skLineSegment(sketch, "E219.25.0", {"start": v(115, 0) * mm, "end": v(125, 0) * mm});
            skLineSegment(sketch, "E219.25.1", {"start": v(125, 0) * mm, "end": v(125, 4) * mm});
            skLineSegment(sketch, "E219.25.2", {"start": v(125, 4) * mm, "end": v(115, 4) * mm});
            skLineSegment(sketch, "E219.25.3", {"start": v(115, 4) * mm, "end": v(115, 0) * mm});
            skLineSegment(sketch, "E219.26.0", {"start": v(146, 4) * mm, "end": v(125, 4) * mm});
            skLineSegment(sketch, "E219.26.1", {"start": v(125, 4) * mm, "end": v(125, 0) * mm});
            skLineSegment(sketch, "E219.26.2", {"start": v(125, 0) * mm, "end": v(146, 0) * mm});
            skLineSegment(sketch, "E219.26.3", {"start": v(146, 0) * mm, "end": v(146, 4) * mm});
            skLineSegment(sketch, "E220.bottom", {"start": v(-146, 4) * mm, "end": v(146, 4) * mm});
            skLineSegment(sketch, "E221.0.0", {"start": v(-150, 0) * mm, "end": v(-146, 0) * mm});
            skLineSegment(sketch, "E221.0.1", {"start": v(-146, 0) * mm, "end": v(-146, 4) * mm});
            skLineSegment(sketch, "E221.0.2", {"start": v(-146, 4) * mm, "end": v(-150, 4) * mm});
            skLineSegment(sketch, "E221.0.3", {"start": v(-150, 4) * mm, "end": v(-150, 0) * mm});
            skLineSegment(sketch, "E222.0.0", {"start": v(150, 4) * mm, "end": v(146, 4) * mm});
            skLineSegment(sketch, "E222.0.1", {"start": v(146, 4) * mm, "end": v(146, 0) * mm});
            skLineSegment(sketch, "E222.0.2", {"start": v(146, 0) * mm, "end": v(150, 0) * mm});
            skLineSegment(sketch, "E222.0.3", {"start": v(150, 0) * mm, "end": v(150, 4) * mm});
            skLineSegment(sketch, "E223.bottom", {"start": v(-150, 0) * mm, "end": v(150, 0) * mm});
            skLineSegment(sketch, "E223.left", {"start": v(-150, 0) * mm, "end": v(-150, 4) * mm});
            skLineSegment(sketch, "E224", {"start": v(150, 50) * mm, "end": v(146, 50) * mm});
            skLineSegment(sketch, "E225", {"start": v(150, 45) * mm, "end": v(146, 45) * mm});
            skLineSegment(sketch, "E226.MirrorCS", {"start": v(150, 55) * mm, "end": v(146, 55) * mm});
            skLineSegment(sketch, "E227.0.1.0", {"start": v(150, 25) * mm, "end": v(146, 25) * mm});
            skLineSegment(sketch, "E227.0.1.1", {"start": v(150, 35) * mm, "end": v(146, 35) * mm});
            skLineSegment(sketch, "E227.direction1", {"start": v(146, 45) * mm, "end": v(171, 45) * mm, "construction": true});
            skLineSegment(sketch, "E227.direction2", {"start": v(146, 45) * mm, "end": v(146, 25) * mm, "construction": true});
            skLineSegment(sketch, "E228.trimOffspring", {"start": v(150, 45) * mm, "end": v(150, 55) * mm});
            skLineSegment(sketch, "E229.trimOffspring", {"start": v(150, 25) * mm, "end": v(150, 35) * mm});
            skLineSegment(sketch, "E230", {"start": v(146, 100) * mm, "end": v(146, 4) * mm});
            skLineSegment(sketch, "E231.trimOffspring", {"start": v(150, 4) * mm, "end": v(150, 0) * mm});
            skLineSegment(sketch, "E232.trimOffspring", {"start": v(150, 35) * mm, "end": v(150, 25) * mm});
            skLineSegment(sketch, "E233.MirrorCS", {"start": v(150, 75) * mm, "end": v(150, 65) * mm});
            skLineSegment(sketch, "E234.MirrorCS", {"start": v(150, 75) * mm, "end": v(146, 75) * mm});
            skLineSegment(sketch, "E235.MirrorCS", {"start": v(150, 65) * mm, "end": v(146, 65) * mm});
            skLineSegment(sketch, "E236.trimOffspring", {"start": v(150, 55) * mm, "end": v(150, 45) * mm});
            skPoint(sketch, "E237.trimOffspring.end.orphan", {"position": v(150, 100) * mm});
            skLineSegment(sketch, "E238.trimOffspring", {"start": v(146, 100) * mm, "end": v(150, 100) * mm});
            skLineSegment(sketch, "E239", {"start": v(-150, 100) * mm, "end": v(150, 100) * mm});
            skLineSegment(sketch, "E240", {"start": v(0, 0) * mm, "end": v(0, 100) * mm});
            skLineSegment(sketch, "E241.MirrorCS", {"start": v(-150, 45) * mm, "end": v(-146, 45) * mm});
            skLineSegment(sketch, "E242.MirrorCS", {"start": v(-150, 65) * mm, "end": v(-146, 65) * mm});
            skLineSegment(sketch, "E243.MirrorCS", {"start": v(-150, 75) * mm, "end": v(-146, 75) * mm});
            skLineSegment(sketch, "E244.MirrorCS", {"start": v(-150, 25) * mm, "end": v(-146, 25) * mm});
            skLineSegment(sketch, "E245.MirrorCS", {"start": v(-150, 25) * mm, "end": v(-150, 35) * mm});
            skLineSegment(sketch, "E246.MirrorCS", {"start": v(-150, 50) * mm, "end": v(-146, 50) * mm});
            skLineSegment(sketch, "E247.MirrorCS", {"start": v(-150, 35) * mm, "end": v(-146, 35) * mm});
            skLineSegment(sketch, "E248.MirrorCS", {"start": v(-150, 55) * mm, "end": v(-146, 55) * mm});
            skLineSegment(sketch, "E249.MirrorCS", {"start": v(-150, 55) * mm, "end": v(-150, 45) * mm});
            skLineSegment(sketch, "E250.MirrorCS", {"start": v(-146, 45) * mm, "end": v(-171, 45) * mm, "construction": true});
            skLineSegment(sketch, "E251.MirrorCS", {"start": v(-150, 35) * mm, "end": v(-150, 25) * mm});
            skLineSegment(sketch, "E252.MirrorCS", {"start": v(-146, 45) * mm, "end": v(-146, 25) * mm, "construction": true});
            skLineSegment(sketch, "E253.MirrorCS", {"start": v(-150, 45) * mm, "end": v(-150, 55) * mm});
            skLineSegment(sketch, "E254.MirrorCS", {"start": v(-150, 75) * mm, "end": v(-150, 65) * mm});
            skLineSegment(sketch, "E255", {"start": v(-146, 100) * mm, "end": v(-146, 4) * mm});
            skLineSegment(sketch, "E256.trimOffspring", {"start": v(-150, 45) * mm, "end": v(-150, 50) * mm});
            skLineSegment(sketch, "E257.trimOffspring", {"start": v(-150, 65) * mm, "end": v(-150, 75) * mm});
            skLineSegment(sketch, "E258.MirrorCS", {"start": v(150, 96) * mm, "end": v(150, 100) * mm});
            skLineSegment(sketch, "E259.MirrorCS", {"start": v(146, 96) * mm, "end": v(146, 100) * mm});
            skLineSegment(sketch, "E260.MirrorCS", {"start": v(-146, 100) * mm, "end": v(-146, 96) * mm});
            skLineSegment(sketch, "E261.MirrorCS", {"start": v(150, 96) * mm, "end": v(146, 96) * mm});
            skLineSegment(sketch, "E262.MirrorCS", {"start": v(150, 100) * mm, "end": v(150, 96) * mm});
            skLineSegment(sketch, "E263.MirrorCS", {"start": v(146, 100) * mm, "end": v(146, 96) * mm});
            skLineSegment(sketch, "E264.MirrorCS", {"start": v(-146, 96) * mm, "end": v(-146, 100) * mm});
            skLineSegment(sketch, "E265.MirrorCS", {"start": v(5, 96) * mm, "end": v(5, 100) * mm});
            skLineSegment(sketch, "E266.MirrorCS", {"start": v(-15, 100) * mm, "end": v(-15, 96) * mm});
            skLineSegment(sketch, "E267.MirrorCS", {"start": v(-55, 100) * mm, "end": v(-55, 96) * mm});
            skLineSegment(sketch, "E268.MirrorCS", {"start": v(105, 96) * mm, "end": v(105, 100) * mm});
            skLineSegment(sketch, "E269.MirrorCS", {"start": v(65, 96) * mm, "end": v(65, 100) * mm});
            skLineSegment(sketch, "E270.MirrorCS", {"start": v(15, 100) * mm, "end": v(15, 96) * mm});
            skLineSegment(sketch, "E271.MirrorCS", {"start": v(-25, 96) * mm, "end": v(-25, 100) * mm});
            skLineSegment(sketch, "E272.MirrorCS", {"start": v(-65, 96) * mm, "end": v(-65, 100) * mm});
            skLineSegment(sketch, "E273.MirrorCS", {"start": v(115, 100) * mm, "end": v(115, 96) * mm});
            skLineSegment(sketch, "E274.MirrorCS", {"start": v(-45, 100) * mm, "end": v(-45, 96) * mm});
            skLineSegment(sketch, "E275.MirrorCS", {"start": v(-95, 96) * mm, "end": v(-95, 100) * mm});
            skLineSegment(sketch, "E276.MirrorCS", {"start": v(45, 100) * mm, "end": v(45, 96) * mm});
            skLineSegment(sketch, "E277.MirrorCS", {"start": v(125, 100) * mm, "end": v(125, 96) * mm});
            skLineSegment(sketch, "E278.MirrorCS", {"start": v(85, 100) * mm, "end": v(85, 96) * mm});
            skLineSegment(sketch, "E279.MirrorCS", {"start": v(-150, 100) * mm, "end": v(-150, 96) * mm});
            skLineSegment(sketch, "E280.MirrorCS", {"start": v(-85, 100) * mm, "end": v(-85, 96) * mm});
            skLineSegment(sketch, "E281.MirrorCS", {"start": v(-5, 100) * mm, "end": v(-5, 96) * mm});
            skLineSegment(sketch, "E282.MirrorCS", {"start": v(75, 96) * mm, "end": v(75, 100) * mm});
            skLineSegment(sketch, "E283.MirrorCS", {"start": v(-35, 100) * mm, "end": v(-35, 96) * mm});
            skLineSegment(sketch, "E284.MirrorCS", {"start": v(-75, 100) * mm, "end": v(-75, 96) * mm});
            skLineSegment(sketch, "E285.MirrorCS", {"start": v(95, 100) * mm, "end": v(95, 96) * mm});
            skLineSegment(sketch, "E286.MirrorCS", {"start": v(55, 100) * mm, "end": v(55, 96) * mm});
            skLineSegment(sketch, "E287.MirrorCS", {"start": v(-146, 96) * mm, "end": v(-150, 96) * mm});
            skLineSegment(sketch, "E288.MirrorCS", {"start": v(-105, 96) * mm, "end": v(-105, 100) * mm});
            skLineSegment(sketch, "E289.MirrorCS", {"start": v(-125, 100) * mm, "end": v(-125, 96) * mm});
            skLineSegment(sketch, "E290.MirrorCS", {"start": v(-115, 96) * mm, "end": v(-115, 100) * mm});
            skLineSegment(sketch, "E291.MirrorCS", {"start": v(-15, 96) * mm, "end": v(-15, 100) * mm});
            skLineSegment(sketch, "E292.MirrorCS", {"start": v(-55, 96) * mm, "end": v(-55, 100) * mm});
            skLineSegment(sketch, "E293.MirrorCS", {"start": v(115, 96) * mm, "end": v(115, 100) * mm});
            skLineSegment(sketch, "E294.MirrorCS", {"start": v(45, 96) * mm, "end": v(45, 100) * mm});
            skLineSegment(sketch, "E295.MirrorCS", {"start": v(5, 100) * mm, "end": v(5, 96) * mm});
            skLineSegment(sketch, "E296.MirrorCS", {"start": v(125, 96) * mm, "end": v(125, 100) * mm});
            skLineSegment(sketch, "E297.MirrorCS", {"start": v(85, 96) * mm, "end": v(85, 100) * mm});
            skLineSegment(sketch, "E298.MirrorCS", {"start": v(-45, 96) * mm, "end": v(-45, 100) * mm});
            skLineSegment(sketch, "E299.MirrorCS", {"start": v(-85, 96) * mm, "end": v(-85, 100) * mm});
            skLineSegment(sketch, "E300.MirrorCS", {"start": v(-5, 96) * mm, "end": v(-5, 100) * mm});
            skLineSegment(sketch, "E301.MirrorCS", {"start": v(-35, 96) * mm, "end": v(-35, 100) * mm});
            skLineSegment(sketch, "E302.MirrorCS", {"start": v(-75, 96) * mm, "end": v(-75, 100) * mm});
            skLineSegment(sketch, "E303.MirrorCS", {"start": v(-150, 100) * mm, "end": v(-146, 100) * mm});
            skLineSegment(sketch, "E304.MirrorCS", {"start": v(105, 100) * mm, "end": v(105, 96) * mm});
            skLineSegment(sketch, "E305.MirrorCS", {"start": v(65, 100) * mm, "end": v(65, 96) * mm});
            skLineSegment(sketch, "E306.MirrorCS", {"start": v(-25, 100) * mm, "end": v(-25, 96) * mm});
            skLineSegment(sketch, "E307.MirrorCS", {"start": v(-65, 100) * mm, "end": v(-65, 96) * mm});
            skLineSegment(sketch, "E308.MirrorCS", {"start": v(95, 96) * mm, "end": v(95, 100) * mm});
            skLineSegment(sketch, "E309.MirrorCS", {"start": v(55, 96) * mm, "end": v(55, 100) * mm});
            skLineSegment(sketch, "E310.MirrorCS", {"start": v(15, 96) * mm, "end": v(15, 100) * mm});
            skLineSegment(sketch, "E311.MirrorCS", {"start": v(-150, 96) * mm, "end": v(-150, 100) * mm});
            skLineSegment(sketch, "E312.MirrorCS", {"start": v(75, 100) * mm, "end": v(75, 96) * mm});
            skLineSegment(sketch, "E313.MirrorCS", {"start": v(-95, 100) * mm, "end": v(-95, 96) * mm});
            skLineSegment(sketch, "E314.MirrorCS", {"start": v(-105, 100) * mm, "end": v(-105, 96) * mm});
            skLineSegment(sketch, "E315.MirrorCS", {"start": v(-115, 100) * mm, "end": v(-115, 96) * mm});
            skLineSegment(sketch, "E316.MirrorCS", {"start": v(-125, 96) * mm, "end": v(-125, 100) * mm});
            skLineSegment(sketch, "E317.MirrorCS", {"start": v(35, 96) * mm, "end": v(35, 100) * mm});
            skLineSegment(sketch, "E318.MirrorCS", {"start": v(25, 100) * mm, "end": v(25, 96) * mm});
            skLineSegment(sketch, "E319.MirrorCS", {"start": v(75, 96) * mm, "end": v(65, 96) * mm});
            skLineSegment(sketch, "E320.MirrorCS", {"start": v(5, 100) * mm, "end": v(15, 100) * mm});
            skLineSegment(sketch, "E321.MirrorCS", {"start": v(-15, 96) * mm, "end": v(-25, 96) * mm});
            skLineSegment(sketch, "E322.MirrorCS", {"start": v(-55, 96) * mm, "end": v(-65, 96) * mm});
            skLineSegment(sketch, "E323.MirrorCS", {"start": v(105, 100) * mm, "end": v(115, 100) * mm});
            skLineSegment(sketch, "E324.MirrorCS", {"start": v(65, 100) * mm, "end": v(75, 100) * mm});
            skLineSegment(sketch, "E325.MirrorCS", {"start": v(35, 100) * mm, "end": v(45, 100) * mm});
            skLineSegment(sketch, "E326.MirrorCS", {"start": v(-5, 96) * mm, "end": v(-15, 96) * mm});
            skLineSegment(sketch, "E327.MirrorCS", {"start": v(115, 100) * mm, "end": v(125, 100) * mm});
            skLineSegment(sketch, "E328.MirrorCS", {"start": v(75, 100) * mm, "end": v(85, 100) * mm});
            skLineSegment(sketch, "E329.MirrorCS", {"start": v(-45, 96) * mm, "end": v(-55, 96) * mm});
            skLineSegment(sketch, "E330.MirrorCS", {"start": v(-95, 100) * mm, "end": v(-85, 100) * mm});
            skLineSegment(sketch, "E331.MirrorCS", {"start": v(125, 96) * mm, "end": v(115, 96) * mm});
            skLineSegment(sketch, "E332.MirrorCS", {"start": v(85, 96) * mm, "end": v(75, 96) * mm});
            skLineSegment(sketch, "E333.MirrorCS", {"start": v(45, 96) * mm, "end": v(35, 96) * mm});
            skLineSegment(sketch, "E334.MirrorCS", {"start": v(-85, 96) * mm, "end": v(-95, 96) * mm});
            skLineSegment(sketch, "E335.MirrorCS", {"start": v(55, 96) * mm, "end": v(45, 96) * mm});
            skLineSegment(sketch, "E336.MirrorCS", {"start": v(-5, 100) * mm, "end": v(5, 100) * mm});
            skLineSegment(sketch, "E337.MirrorCS", {"start": v(146, 96) * mm, "end": v(125, 96) * mm});
            skLineSegment(sketch, "E338.MirrorCS", {"start": v(95, 96) * mm, "end": v(85, 96) * mm});
            skLineSegment(sketch, "E339.MirrorCS", {"start": v(5, 96) * mm, "end": v(-5, 96) * mm});
            skLineSegment(sketch, "E340.MirrorCS", {"start": v(-35, 96) * mm, "end": v(-45, 96) * mm});
            skLineSegment(sketch, "E341.MirrorCS", {"start": v(-75, 96) * mm, "end": v(-85, 96) * mm});
            skLineSegment(sketch, "E342.MirrorCS", {"start": v(-25, 96) * mm, "end": v(-35, 96) * mm});
            skLineSegment(sketch, "E343.MirrorCS", {"start": v(-65, 96) * mm, "end": v(-75, 96) * mm});
            skLineSegment(sketch, "E344.MirrorCS", {"start": v(-15, 100) * mm, "end": v(-5, 100) * mm});
            skLineSegment(sketch, "E345.MirrorCS", {"start": v(-55, 100) * mm, "end": v(-45, 100) * mm});
            skLineSegment(sketch, "E346.MirrorCS", {"start": v(-45, 100) * mm, "end": v(-35, 100) * mm});
            skLineSegment(sketch, "E347.MirrorCS", {"start": v(-85, 100) * mm, "end": v(-75, 100) * mm});
            skLineSegment(sketch, "E348.MirrorCS", {"start": v(45, 100) * mm, "end": v(55, 100) * mm});
            skLineSegment(sketch, "E349.MirrorCS", {"start": v(125, 100) * mm, "end": v(146, 100) * mm});
            skLineSegment(sketch, "E350.MirrorCS", {"start": v(85, 100) * mm, "end": v(95, 100) * mm});
            skLineSegment(sketch, "E351.MirrorCS", {"start": v(-146, 96) * mm, "end": v(146, 96) * mm});
            skLineSegment(sketch, "E352.MirrorCS", {"start": v(95, 100) * mm, "end": v(105, 100) * mm});
            skLineSegment(sketch, "E353.MirrorCS", {"start": v(55, 100) * mm, "end": v(65, 100) * mm});
            skLineSegment(sketch, "E354.MirrorCS", {"start": v(15, 100) * mm, "end": v(25, 100) * mm});
            skLineSegment(sketch, "E355.MirrorCS", {"start": v(-35, 100) * mm, "end": v(-25, 100) * mm});
            skLineSegment(sketch, "E356.MirrorCS", {"start": v(-75, 100) * mm, "end": v(-65, 100) * mm});
            skLineSegment(sketch, "E357.MirrorCS", {"start": v(105, 96) * mm, "end": v(95, 96) * mm});
            skLineSegment(sketch, "E358.MirrorCS", {"start": v(65, 96) * mm, "end": v(55, 96) * mm});
            skLineSegment(sketch, "E359.MirrorCS", {"start": v(25, 96) * mm, "end": v(15, 96) * mm});
            skLineSegment(sketch, "E360.MirrorCS", {"start": v(-25, 100) * mm, "end": v(-15, 100) * mm});
            skLineSegment(sketch, "E361.MirrorCS", {"start": v(-65, 100) * mm, "end": v(-55, 100) * mm});
            skLineSegment(sketch, "E362.MirrorCS", {"start": v(115, 96) * mm, "end": v(105, 96) * mm});
            skLineSegment(sketch, "E363.MirrorCS", {"start": v(15, 96) * mm, "end": v(5, 96) * mm});
            skLineSegment(sketch, "E364.MirrorCS", {"start": v(-95, 96) * mm, "end": v(-105, 96) * mm});
            skLineSegment(sketch, "E365.MirrorCS", {"start": v(-146, 100) * mm, "end": v(-125, 100) * mm});
            skLineSegment(sketch, "E366.MirrorCS", {"start": v(-125, 96) * mm, "end": v(-146, 96) * mm});
            skLineSegment(sketch, "E367.MirrorCS", {"start": v(-105, 96) * mm, "end": v(-115, 96) * mm});
            skLineSegment(sketch, "E368.MirrorCS", {"start": v(-115, 100) * mm, "end": v(-105, 100) * mm});
            skLineSegment(sketch, "E369.MirrorCS", {"start": v(-125, 100) * mm, "end": v(-115, 100) * mm});
            skLineSegment(sketch, "E370.MirrorCS", {"start": v(-115, 96) * mm, "end": v(-125, 96) * mm});
            skLineSegment(sketch, "E371.MirrorCS", {"start": v(-105, 100) * mm, "end": v(-95, 100) * mm});
            skSolve(sketch);
        }
        {
            var Q0;
            {var subQ0=sQuery(id+"F6.wireOp",EDGE,"E227.0.1.0");Q0=makeQuery(id+"F6.imprint","IMPRINT",FACE,{"disambiguationData":[TD([[makeQuery(id+"F6.imprint","IMPRINT",EDGE,{"derivedFrom":subQ0}),-1.0]])]});}
            var Q1;
            Q1=makeQuery(id+"F6.imprint","IMPRINT",FACE,{"disambiguationData":[TD([[makeQuery(id+"F6.imprint","IMPRINT",EDGE,{"derivedFrom":sQuery(id+"F6.wireOp",EDGE,"E233.MirrorCS")}),-1.0]])]});
            var Q2;
            {var subQ0=sQuery(id+"F6.wireOp",EDGE,"E242.MirrorCS");Q2=makeQuery(id+"F6.imprint","IMPRINT",FACE,{"disambiguationData":[TD([[makeQuery(id+"F6.imprint","IMPRINT",EDGE,{"derivedFrom":subQ0}),1.0]])]});}
            var Q3;
            {var subQ0=sQuery(id+"F6.wireOp",EDGE,"E244.MirrorCS");Q3=makeQuery(id+"F6.imprint","IMPRINT",FACE,{"disambiguationData":[TD([[makeQuery(id+"F6.imprint","IMPRINT",EDGE,{"derivedFrom":subQ0}),1.0]])]});}
            var Q4;
            {var subQ0=sQuery(id+"F6.wireOp",EDGE,"E224");Q4=makeQuery(id+"F6.imprint","IMPRINT",FACE,{"disambiguationData":[TD([[makeQuery(id+"F6.imprint","IMPRINT",EDGE,{"derivedFrom":subQ0}),1.0]])]});}
            var Q5;
            {var subQ0=sQuery(id+"F6.wireOp",EDGE,"E224");Q5=makeQuery(id+"F6.imprint","IMPRINT",FACE,{"disambiguationData":[TD([[makeQuery(id+"F6.imprint","IMPRINT",EDGE,{"derivedFrom":subQ0}),-1.0]])]});}
            var Q6;
            {var subQ0=sQuery(id+"F6.wireOp",EDGE,"E241.MirrorCS");Q6=makeQuery(id+"F6.imprint","IMPRINT",FACE,{"disambiguationData":[TD([[makeQuery(id+"F6.imprint","IMPRINT",EDGE,{"derivedFrom":subQ0}),1.0]])]});}
            var Q7;
            {var subQ0=sQuery(id+"F6.wireOp",EDGE,"E246.MirrorCS");Q7=makeQuery(id+"F6.imprint","IMPRINT",FACE,{"disambiguationData":[TD([[makeQuery(id+"F6.imprint","IMPRINT",EDGE,{"derivedFrom":subQ0}),1.0]])]});}
            var Q8;
            {var subQ6=sQuery(id+"F6.wireOp",EDGE,"E220.bottom");var subQ7=makeQuery(id+"F6.imprint","INTERSECT",VERTEX,{"derivedFrom":[sQuery(id+"F6.wireOp",EDGE,"E219.2.1"),subQ6]});Q8=makeQuery(id+"F6.imprint","IMPRINT",FACE,{"disambiguationData":[TD([[makeQuery(id+"F6.imprint","IMPRINT",EDGE,{"disambiguationData":[TD([[subQ7,1.0]])],"derivedFrom":subQ6}),1.0]])]});}
            var Q9;
            Q9=makeQuery(id+"F6.imprint","IMPRINT",FACE,{"disambiguationData":[TD([[makeQuery(id+"F6.imprint","IMPRINT",EDGE,{"derivedFrom":sQuery(id+"F6.wireOp",EDGE,"E264.MirrorCS")}),-1.0]])]});
            var Q10;
            Q10=makeQuery(id+"F6.imprint","IMPRINT",FACE,{"disambiguationData":[TD([[makeQuery(id+"F6.imprint","IMPRINT",EDGE,{"derivedFrom":sQuery(id+"F6.wireOp",EDGE,"E314.MirrorCS")}),-1.0]])]});
            var Q11;
            {var subQ0=sQuery(id+"F6.wireOp",EDGE,"E299.MirrorCS");Q11=makeQuery(id+"F6.imprint","IMPRINT",FACE,{"disambiguationData":[TD([[makeQuery(id+"F6.imprint","IMPRINT",EDGE,{"derivedFrom":subQ0}),1.0]])]});}
            var Q12;
            {var subQ0=sQuery(id+"F6.wireOp",EDGE,"E302.MirrorCS");Q12=makeQuery(id+"F6.imprint","IMPRINT",FACE,{"disambiguationData":[TD([[makeQuery(id+"F6.imprint","IMPRINT",EDGE,{"derivedFrom":subQ0}),-1.0]])]});}
            var Q13;
            {var subQ0=sQuery(id+"F6.wireOp",EDGE,"E292.MirrorCS");Q13=makeQuery(id+"F6.imprint","IMPRINT",FACE,{"disambiguationData":[TD([[makeQuery(id+"F6.imprint","IMPRINT",EDGE,{"derivedFrom":subQ0}),-1.0]])]});}
            var Q14;
            {var subQ0=sQuery(id+"F6.wireOp",EDGE,"E301.MirrorCS");Q14=makeQuery(id+"F6.imprint","IMPRINT",FACE,{"disambiguationData":[TD([[makeQuery(id+"F6.imprint","IMPRINT",EDGE,{"derivedFrom":subQ0}),-1.0]])]});}
            var Q15;
            {var subQ0=sQuery(id+"F6.wireOp",EDGE,"E291.MirrorCS");Q15=makeQuery(id+"F6.imprint","IMPRINT",FACE,{"disambiguationData":[TD([[makeQuery(id+"F6.imprint","IMPRINT",EDGE,{"derivedFrom":subQ0}),-1.0]])]});}
            var Q16;
            {var subQ10=sQuery(id+"F6.wireOp",EDGE,"E357.MirrorCS");Q16=makeQuery(id+"F6.imprint","IMPRINT",FACE,{"disambiguationData":[TD([[makeQuery(id+"F6.imprint","IMPRINT",EDGE,{"derivedFrom":subQ10}),1.0]])]});}
            var Q17;
            {var subQ0=sQuery(id+"F6.wireOp",EDGE,"E295.MirrorCS");Q17=makeQuery(id+"F6.imprint","IMPRINT",FACE,{"disambiguationData":[TD([[makeQuery(id+"F6.imprint","IMPRINT",EDGE,{"derivedFrom":subQ0}),1.0]])]});}
            var Q18;
            {var subQ0=sQuery(id+"F6.wireOp",EDGE,"E317.MirrorCS");Q18=makeQuery(id+"F6.imprint","IMPRINT",FACE,{"disambiguationData":[TD([[makeQuery(id+"F6.imprint","IMPRINT",EDGE,{"derivedFrom":subQ0}),1.0]])]});}
            var Q19;
            {var subQ0=sQuery(id+"F6.wireOp",EDGE,"E294.MirrorCS");Q19=makeQuery(id+"F6.imprint","IMPRINT",FACE,{"disambiguationData":[TD([[makeQuery(id+"F6.imprint","IMPRINT",EDGE,{"derivedFrom":subQ0}),-1.0]])]});}
            var Q20;
            {var subQ0=sQuery(id+"F6.wireOp",EDGE,"E305.MirrorCS");Q20=makeQuery(id+"F6.imprint","IMPRINT",FACE,{"disambiguationData":[TD([[makeQuery(id+"F6.imprint","IMPRINT",EDGE,{"derivedFrom":subQ0}),1.0]])]});}
            var Q21;
            {var subQ0=sQuery(id+"F6.wireOp",EDGE,"E297.MirrorCS");Q21=makeQuery(id+"F6.imprint","IMPRINT",FACE,{"disambiguationData":[TD([[makeQuery(id+"F6.imprint","IMPRINT",EDGE,{"derivedFrom":subQ0}),-1.0]])]});}
            var Q22;
            {var subQ0=sQuery(id+"F6.wireOp",EDGE,"E293.MirrorCS");Q22=makeQuery(id+"F6.imprint","IMPRINT",FACE,{"disambiguationData":[TD([[makeQuery(id+"F6.imprint","IMPRINT",EDGE,{"derivedFrom":subQ0}),1.0]])]});}
            var Q23;
            {var subQ0=sQuery(id+"F6.wireOp",EDGE,"E263.MirrorCS");Q23=makeQuery(id+"F6.imprint","IMPRINT",FACE,{"disambiguationData":[TD([[makeQuery(id+"F6.imprint","IMPRINT",EDGE,{"derivedFrom":subQ0}),-1.0]])]});}
            extrude(context, id + "F7", {"entities" : qUnion([Q0, Q1, Q2, Q3, Q4, Q5, Q6, Q7, Q8, Q9, Q10, Q11, Q12, Q13, Q14, Q15, Q16, Q17, Q18, Q19, Q20, Q21, Q22, Q23]), "oppositeDirection" : true, "depth" : 4 * mm});
        }
        {
            var Q0;
            Q0=makeQuery(id+"F5.opExtrude","CAP_FACE",FACE,{"disambiguationData":[OSD([sQuery(id+"F4.wireOp",EDGE,"E216.4.0"),sQuery(id+"F4.wireOp",EDGE,"E216.4.2"),sQuery(id+"F4.wireOp",EDGE,"E216.4.3"),sQuery(id+"F4.wireOp",EDGE,"E216.5.3")])],"isStart":true});
            var sketch = newSketch(context, id + "F8", { "sketchPlane" : qUnion([Q0])});
            skLineSegment(sketch, "E372.0.0", {"start": v(-85, 0) * mm, "end": v(-85, 4) * mm});
            skLineSegment(sketch, "E372.0.1", {"start": v(-85, 4) * mm, "end": v(-100, 4) * mm});
            skLineSegment(sketch, "E372.0.2", {"start": v(-100, 4) * mm, "end": v(-100, 0) * mm});
            skLineSegment(sketch, "E372.0.3", {"start": v(-100, 0) * mm, "end": v(-85, 0) * mm});
            skLineSegment(sketch, "E372.1.0", {"start": v(-85, 0) * mm, "end": v(-75, 0) * mm});
            skLineSegment(sketch, "E372.1.1", {"start": v(-75, 0) * mm, "end": v(-75, 4) * mm});
            skLineSegment(sketch, "E372.1.2", {"start": v(-75, 4) * mm, "end": v(-85, 4) * mm});
            skLineSegment(sketch, "E372.1.3", {"start": v(-85, 4) * mm, "end": v(-85, 0) * mm});
            skLineSegment(sketch, "E372.2.0", {"start": v(-65, 0) * mm, "end": v(-65, 4) * mm});
            skLineSegment(sketch, "E372.2.1", {"start": v(-65, 4) * mm, "end": v(-75, 4) * mm});
            skLineSegment(sketch, "E372.2.2", {"start": v(-75, 4) * mm, "end": v(-75, 0) * mm});
            skLineSegment(sketch, "E372.2.3", {"start": v(-75, 0) * mm, "end": v(-65, 0) * mm});
            skLineSegment(sketch, "E372.3.0", {"start": v(-65, 0) * mm, "end": v(-55, 0) * mm});
            skLineSegment(sketch, "E372.3.1", {"start": v(-55, 0) * mm, "end": v(-55, 4) * mm});
            skLineSegment(sketch, "E372.3.2", {"start": v(-55, 4) * mm, "end": v(-65, 4) * mm});
            skLineSegment(sketch, "E372.3.3", {"start": v(-65, 4) * mm, "end": v(-65, 0) * mm});
            skLineSegment(sketch, "E372.4.0", {"start": v(-45, 0) * mm, "end": v(-35, 0) * mm});
            skLineSegment(sketch, "E372.4.1", {"start": v(-35, 0) * mm, "end": v(-35, 4) * mm});
            skLineSegment(sketch, "E372.4.2", {"start": v(-35, 4) * mm, "end": v(-45, 4) * mm});
            skLineSegment(sketch, "E372.4.3", {"start": v(-45, 4) * mm, "end": v(-45, 0) * mm});
            skLineSegment(sketch, "E372.5.0", {"start": v(-25, 0) * mm, "end": v(-25, 4) * mm});
            skLineSegment(sketch, "E372.5.1", {"start": v(-25, 4) * mm, "end": v(-35, 4) * mm});
            skLineSegment(sketch, "E372.5.2", {"start": v(-35, 4) * mm, "end": v(-35, 0) * mm});
            skLineSegment(sketch, "E372.5.3", {"start": v(-35, 0) * mm, "end": v(-25, 0) * mm});
            skLineSegment(sketch, "E372.6.0", {"start": v(-25, 0) * mm, "end": v(-15, 0) * mm});
            skLineSegment(sketch, "E372.6.1", {"start": v(-15, 0) * mm, "end": v(-15, 4) * mm});
            skLineSegment(sketch, "E372.6.2", {"start": v(-15, 4) * mm, "end": v(-25, 4) * mm});
            skLineSegment(sketch, "E372.6.3", {"start": v(-25, 4) * mm, "end": v(-25, 0) * mm});
            skLineSegment(sketch, "E372.7.0", {"start": v(-5, 4) * mm, "end": v(-15, 4) * mm});
            skLineSegment(sketch, "E372.7.1", {"start": v(-15, 4) * mm, "end": v(-15, 0) * mm});
            skLineSegment(sketch, "E372.7.2", {"start": v(-15, 0) * mm, "end": v(-5, 0) * mm});
            skLineSegment(sketch, "E372.7.3", {"start": v(-5, 0) * mm, "end": v(-5, 4) * mm});
            skLineSegment(sketch, "E372.9.0", {"start": v(-5, 0) * mm, "end": v(5, 0) * mm});
            skLineSegment(sketch, "E372.9.1", {"start": v(5, 0) * mm, "end": v(5, 4) * mm});
            skLineSegment(sketch, "E372.9.2", {"start": v(5, 4) * mm, "end": v(-5, 4) * mm});
            skLineSegment(sketch, "E372.9.3", {"start": v(-5, 4) * mm, "end": v(-5, 0) * mm});
            skLineSegment(sketch, "E372.10.0", {"start": v(15, 0) * mm, "end": v(15, 4) * mm});
            skLineSegment(sketch, "E372.10.1", {"start": v(15, 4) * mm, "end": v(5, 4) * mm});
            skLineSegment(sketch, "E372.10.2", {"start": v(5, 4) * mm, "end": v(5, 0) * mm});
            skLineSegment(sketch, "E372.10.3", {"start": v(5, 0) * mm, "end": v(15, 0) * mm});
            skLineSegment(sketch, "E372.11.0", {"start": v(15, 0) * mm, "end": v(25, 0) * mm});
            skLineSegment(sketch, "E372.11.1", {"start": v(25, 0) * mm, "end": v(25, 4) * mm});
            skLineSegment(sketch, "E372.11.2", {"start": v(25, 4) * mm, "end": v(15, 4) * mm});
            skLineSegment(sketch, "E372.11.3", {"start": v(15, 4) * mm, "end": v(15, 0) * mm});
            skLineSegment(sketch, "E372.12.0", {"start": v(35, 0) * mm, "end": v(35, 4) * mm});
            skLineSegment(sketch, "E372.12.1", {"start": v(35, 4) * mm, "end": v(25, 4) * mm});
            skLineSegment(sketch, "E372.12.2", {"start": v(25, 4) * mm, "end": v(25, 0) * mm});
            skLineSegment(sketch, "E372.12.3", {"start": v(25, 0) * mm, "end": v(35, 0) * mm});
            skLineSegment(sketch, "E372.13.0", {"start": v(35, 0) * mm, "end": v(45, 0) * mm});
            skLineSegment(sketch, "E372.13.1", {"start": v(45, 0) * mm, "end": v(45, 4) * mm});
            skLineSegment(sketch, "E372.13.2", {"start": v(45, 4) * mm, "end": v(35, 4) * mm});
            skLineSegment(sketch, "E372.13.3", {"start": v(35, 4) * mm, "end": v(35, 0) * mm});
            skLineSegment(sketch, "E372.14.0", {"start": v(55, 0) * mm, "end": v(55, 4) * mm});
            skLineSegment(sketch, "E372.14.1", {"start": v(55, 4) * mm, "end": v(45, 4) * mm});
            skLineSegment(sketch, "E372.14.2", {"start": v(45, 4) * mm, "end": v(45, 0) * mm});
            skLineSegment(sketch, "E372.14.3", {"start": v(45, 0) * mm, "end": v(55, 0) * mm});
            skLineSegment(sketch, "E372.15.0", {"start": v(55, 0) * mm, "end": v(65, 0) * mm});
            skLineSegment(sketch, "E372.15.1", {"start": v(65, 0) * mm, "end": v(65, 4) * mm});
            skLineSegment(sketch, "E372.15.2", {"start": v(65, 4) * mm, "end": v(55, 4) * mm});
            skLineSegment(sketch, "E372.15.3", {"start": v(55, 4) * mm, "end": v(55, 0) * mm});
            skLineSegment(sketch, "E372.16.0", {"start": v(75, 0) * mm, "end": v(75, 4) * mm});
            skLineSegment(sketch, "E372.16.1", {"start": v(75, 4) * mm, "end": v(65, 4) * mm});
            skLineSegment(sketch, "E372.16.2", {"start": v(65, 4) * mm, "end": v(65, 0) * mm});
            skLineSegment(sketch, "E372.16.3", {"start": v(65, 0) * mm, "end": v(75, 0) * mm});
            skLineSegment(sketch, "E372.17.0", {"start": v(75, 0) * mm, "end": v(85, 0) * mm});
            skLineSegment(sketch, "E372.17.1", {"start": v(85, 0) * mm, "end": v(85, 4) * mm});
            skLineSegment(sketch, "E372.17.2", {"start": v(85, 4) * mm, "end": v(75, 4) * mm});
            skLineSegment(sketch, "E372.17.3", {"start": v(75, 4) * mm, "end": v(75, 0) * mm});
            skLineSegment(sketch, "E372.18.0", {"start": v(85, 4) * mm, "end": v(85, 4) * mm});
            skLineSegment(sketch, "E372.18.1", {"start": v(85, 4) * mm, "end": v(85, 0) * mm});
            skLineSegment(sketch, "E372.18.2", {"start": v(85, 0) * mm, "end": v(85, 0) * mm});
            skLineSegment(sketch, "E372.18.3", {"start": v(85, 0) * mm, "end": v(85, 4) * mm});
            skLineSegment(sketch, "E373", {"start": v(-55, 4) * mm, "end": v(-45, 4) * mm});
            skLineSegment(sketch, "E374", {"start": v(-45, 0) * mm, "end": v(-55, 0) * mm});
            skLineSegment(sketch, "E375.0.0", {"start": v(96, 0) * mm, "end": v(100, 0) * mm});
            skLineSegment(sketch, "E375.0.1", {"start": v(100, 0) * mm, "end": v(100, 4) * mm});
            skLineSegment(sketch, "E375.0.2", {"start": v(100, 4) * mm, "end": v(96, 4) * mm});
            skLineSegment(sketch, "E375.0.3", {"start": v(96, 4) * mm, "end": v(96, 0) * mm});
            skLineSegment(sketch, "E376.0.1", {"start": v(-100, 65) * mm, "end": v(-96, 65) * mm});
            skLineSegment(sketch, "E376.0.2", {"start": v(-96, 65) * mm, "end": v(-96, 75) * mm});
            skLineSegment(sketch, "E376.0.3", {"start": v(-96, 75) * mm, "end": v(-100, 75) * mm});
            skLineSegment(sketch, "E376.1.1", {"start": v(-100, 45) * mm, "end": v(-96, 45) * mm});
            skLineSegment(sketch, "E376.1.2", {"start": v(-96, 45) * mm, "end": v(-96, 55) * mm});
            skLineSegment(sketch, "E376.1.3", {"start": v(-96, 55) * mm, "end": v(-100, 55) * mm});
            skLineSegment(sketch, "E376.2.1", {"start": v(-100, 25) * mm, "end": v(-96, 25) * mm});
            skLineSegment(sketch, "E376.2.2", {"start": v(-96, 25) * mm, "end": v(-96, 35) * mm});
            skLineSegment(sketch, "E376.2.3", {"start": v(-96, 35) * mm, "end": v(-100, 35) * mm});
            skLineSegment(sketch, "E377.bottom", {"start": v(-100, 0) * mm, "end": v(100, 0) * mm});
            skLineSegment(sketch, "E377.top", {"start": v(-100, 100) * mm, "end": v(100, 100) * mm});
            skLineSegment(sketch, "E377.left", {"start": v(-100, 0) * mm, "end": v(-100, 25) * mm});
            skLineSegment(sketch, "E377.right", {"start": v(100, 0) * mm, "end": v(100, 25) * mm});
            skLineSegment(sketch, "E378", {"start": v(-96, 0) * mm, "end": v(-96, 100) * mm});
            skLineSegment(sketch, "E379.trimOffspring", {"start": v(-100, 55) * mm, "end": v(-100, 65) * mm});
            skLineSegment(sketch, "E380.trimOffspring", {"start": v(-100, 35) * mm, "end": v(-100, 45) * mm});
            skLineSegment(sketch, "E381.trimOffspring", {"start": v(-100, 75) * mm, "end": v(-100, 100) * mm});
            skLineSegment(sketch, "E382", {"start": v(0, 100) * mm, "end": v(0, 0) * mm, "construction": true});
            skLineSegment(sketch, "E383.MirrorCS", {"start": v(96, 75) * mm, "end": v(100, 75) * mm});
            skLineSegment(sketch, "E384.MirrorCS", {"start": v(100, 65) * mm, "end": v(96, 65) * mm});
            skLineSegment(sketch, "E385.MirrorCS", {"start": v(96, 35) * mm, "end": v(100, 35) * mm});
            skLineSegment(sketch, "E386.MirrorCS", {"start": v(100, 25) * mm, "end": v(96, 25) * mm});
            skLineSegment(sketch, "E387.MirrorCS", {"start": v(100, 45) * mm, "end": v(96, 45) * mm});
            skLineSegment(sketch, "E388.MirrorCS", {"start": v(96, 55) * mm, "end": v(100, 55) * mm});
            skLineSegment(sketch, "E389.MirrorCS", {"start": v(96, 65) * mm, "end": v(96, 75) * mm});
            skLineSegment(sketch, "E390.MirrorCS", {"start": v(96, 25) * mm, "end": v(96, 35) * mm});
            skLineSegment(sketch, "E391.MirrorCS", {"start": v(100, 75) * mm, "end": v(100, 100) * mm});
            skLineSegment(sketch, "E392.MirrorCS", {"start": v(100, 55) * mm, "end": v(100, 65) * mm});
            skLineSegment(sketch, "E393.MirrorCS", {"start": v(100, 35) * mm, "end": v(100, 45) * mm});
            skLineSegment(sketch, "E394.MirrorCS", {"start": v(96, 45) * mm, "end": v(96, 55) * mm});
            skLineSegment(sketch, "E395", {"start": v(0, 50) * mm, "end": v(44.96, 50) * mm, "construction": true});
            skLineSegment(sketch, "E396.MirrorCS", {"start": v(25, 96) * mm, "end": v(15, 96) * mm});
            skLineSegment(sketch, "E397.MirrorCS", {"start": v(25, 96) * mm, "end": v(25, 100) * mm});
            skLineSegment(sketch, "E398.MirrorCS", {"start": v(15, 100) * mm, "end": v(15, 96) * mm});
            skLineSegment(sketch, "E399.MirrorCS", {"start": v(35, 100) * mm, "end": v(35, 96) * mm});
            skLineSegment(sketch, "E400.MirrorCS", {"start": v(45, 96) * mm, "end": v(35, 96) * mm});
            skLineSegment(sketch, "E401.MirrorCS", {"start": v(45, 96) * mm, "end": v(45, 100) * mm});
            skLineSegment(sketch, "E402.MirrorCS", {"start": v(55, 100) * mm, "end": v(55, 96) * mm});
            skLineSegment(sketch, "E403.MirrorCS", {"start": v(65, 96) * mm, "end": v(55, 96) * mm});
            skLineSegment(sketch, "E404.MirrorCS", {"start": v(65, 96) * mm, "end": v(65, 100) * mm});
            skLineSegment(sketch, "E405.MirrorCS", {"start": v(75, 100) * mm, "end": v(75, 96) * mm});
            skLineSegment(sketch, "E406.MirrorCS", {"start": v(85, 96) * mm, "end": v(75, 96) * mm});
            skLineSegment(sketch, "E407.MirrorCS", {"start": v(85, 96) * mm, "end": v(85, 100) * mm});
            skLineSegment(sketch, "E408.MirrorCS", {"start": v(5, 96) * mm, "end": v(-5, 96) * mm});
            skLineSegment(sketch, "E409.MirrorCS", {"start": v(5, 96) * mm, "end": v(5, 100) * mm});
            skLineSegment(sketch, "E410.MirrorCS", {"start": v(-5, 100) * mm, "end": v(-5, 96) * mm});
            skLineSegment(sketch, "E411.MirrorCS", {"start": v(-15, 96) * mm, "end": v(-15, 100) * mm});
            skLineSegment(sketch, "E412.MirrorCS", {"start": v(-15, 96) * mm, "end": v(-25, 96) * mm});
            skLineSegment(sketch, "E413.MirrorCS", {"start": v(-25, 100) * mm, "end": v(-25, 96) * mm});
            skLineSegment(sketch, "E414.MirrorCS", {"start": v(-35, 96) * mm, "end": v(-35, 100) * mm});
            skLineSegment(sketch, "E415.MirrorCS", {"start": v(-35, 96) * mm, "end": v(-45, 96) * mm});
            skLineSegment(sketch, "E416.MirrorCS", {"start": v(-45, 96) * mm, "end": v(-45, 100) * mm});
            skLineSegment(sketch, "E417.MirrorCS", {"start": v(-55, 100) * mm, "end": v(-55, 96) * mm});
            skLineSegment(sketch, "E418.MirrorCS", {"start": v(-55, 96) * mm, "end": v(-65, 96) * mm});
            skLineSegment(sketch, "E419.MirrorCS", {"start": v(-65, 100) * mm, "end": v(-65, 96) * mm});
            skLineSegment(sketch, "E420.MirrorCS", {"start": v(-75, 96) * mm, "end": v(-75, 100) * mm});
            skLineSegment(sketch, "E421.MirrorCS", {"start": v(-75, 96) * mm, "end": v(-85, 96) * mm});
            skLineSegment(sketch, "E422.MirrorCS", {"start": v(-85, 96) * mm, "end": v(-85, 100) * mm});
            skLineSegment(sketch, "E423", {"start": v(85, 4) * mm, "end": v(96, 4) * mm});
            skLineSegment(sketch, "E424", {"start": v(-75, 96) * mm, "end": v(-65, 96) * mm});
            skLineSegment(sketch, "E425", {"start": v(-55, 96) * mm, "end": v(-45, 96) * mm});
            skLineSegment(sketch, "E426", {"start": v(-35, 96) * mm, "end": v(-25, 96) * mm});
            skLineSegment(sketch, "E427", {"start": v(-15, 96) * mm, "end": v(-5, 96) * mm});
            skLineSegment(sketch, "E428", {"start": v(5, 96) * mm, "end": v(15, 96) * mm});
            skLineSegment(sketch, "E429", {"start": v(25, 96) * mm, "end": v(35, 96) * mm});
            skLineSegment(sketch, "E430", {"start": v(45, 96) * mm, "end": v(55, 96) * mm});
            skLineSegment(sketch, "E431", {"start": v(65, 96) * mm, "end": v(75, 96) * mm});
            skLineSegment(sketch, "E432", {"start": v(85, 96) * mm, "end": v(100, 96) * mm});
            skLineSegment(sketch, "E433", {"start": v(-85, 96) * mm, "end": v(-96, 96) * mm});
            skSolve(sketch);
        }
        {
            var Q0;
            {var subQ0=sQuery(id+"F8.wireOp",EDGE,"E376.0.1");Q0=makeQuery(id+"F8.imprint","IMPRINT",FACE,{"disambiguationData":[TD([[makeQuery(id+"F8.imprint","IMPRINT",EDGE,{"derivedFrom":subQ0}),-1.0]])]});}
            var Q1;
            {var subQ0=sQuery(id+"F8.wireOp",EDGE,"E376.0.3");Q1=makeQuery(id+"F8.imprint","IMPRINT",FACE,{"disambiguationData":[TD([[makeQuery(id+"F8.imprint","IMPRINT",EDGE,{"derivedFrom":subQ0}),-1.0]])]});}
            var Q2;
            {var subQ0=sQuery(id+"F8.wireOp",EDGE,"E376.1.1");Q2=makeQuery(id+"F8.imprint","IMPRINT",FACE,{"disambiguationData":[TD([[makeQuery(id+"F8.imprint","IMPRINT",EDGE,{"derivedFrom":subQ0}),-1.0]])]});}
            var Q3;
            {var subQ5=sQuery(id+"F8.wireOp",EDGE,"E376.2.1");Q3=makeQuery(id+"F8.imprint","IMPRINT",FACE,{"disambiguationData":[TD([[makeQuery(id+"F8.imprint","IMPRINT",EDGE,{"derivedFrom":subQ5}),-1.0]])]});}
            var Q4;
            {var subQ11=sQuery(id+"F8.wireOp",EDGE,"E372.1.2");Q4=makeQuery(id+"F8.imprint","IMPRINT",FACE,{"disambiguationData":[TD([[makeQuery(id+"F8.imprint","IMPRINT",EDGE,{"derivedFrom":subQ11}),-1.0]])]});}
            var Q5;
            {var subQ4=sQuery(id+"F8.wireOp",EDGE,"E422.MirrorCS");Q5=makeQuery(id+"F8.imprint","IMPRINT",FACE,{"disambiguationData":[TD([[makeQuery(id+"F8.imprint","IMPRINT",EDGE,{"derivedFrom":subQ4}),1.0]])]});}
            var Q6;
            {var subQ0=sQuery(id+"F8.wireOp",EDGE,"E419.MirrorCS");Q6=makeQuery(id+"F8.imprint","IMPRINT",FACE,{"disambiguationData":[TD([[makeQuery(id+"F8.imprint","IMPRINT",EDGE,{"derivedFrom":subQ0}),-1.0]])]});}
            var Q7;
            {var subQ0=sQuery(id+"F8.wireOp",EDGE,"E416.MirrorCS");Q7=makeQuery(id+"F8.imprint","IMPRINT",FACE,{"disambiguationData":[TD([[makeQuery(id+"F8.imprint","IMPRINT",EDGE,{"derivedFrom":subQ0}),1.0]])]});}
            var Q8;
            {var subQ0=sQuery(id+"F8.wireOp",EDGE,"E413.MirrorCS");Q8=makeQuery(id+"F8.imprint","IMPRINT",FACE,{"disambiguationData":[TD([[makeQuery(id+"F8.imprint","IMPRINT",EDGE,{"derivedFrom":subQ0}),-1.0]])]});}
            var Q9;
            {var subQ0=sQuery(id+"F8.wireOp",EDGE,"E410.MirrorCS");Q9=makeQuery(id+"F8.imprint","IMPRINT",FACE,{"disambiguationData":[TD([[makeQuery(id+"F8.imprint","IMPRINT",EDGE,{"derivedFrom":subQ0}),-1.0]])]});}
            var Q10;
            {var subQ0=sQuery(id+"F8.wireOp",EDGE,"E398.MirrorCS");Q10=makeQuery(id+"F8.imprint","IMPRINT",FACE,{"disambiguationData":[TD([[makeQuery(id+"F8.imprint","IMPRINT",EDGE,{"derivedFrom":subQ0}),-1.0]])]});}
            var Q11;
            {var subQ0=sQuery(id+"F8.wireOp",EDGE,"E397.MirrorCS");Q11=makeQuery(id+"F8.imprint","IMPRINT",FACE,{"disambiguationData":[TD([[makeQuery(id+"F8.imprint","IMPRINT",EDGE,{"derivedFrom":subQ0}),-1.0]])]});}
            var Q12;
            {var subQ0=sQuery(id+"F8.wireOp",EDGE,"E401.MirrorCS");Q12=makeQuery(id+"F8.imprint","IMPRINT",FACE,{"disambiguationData":[TD([[makeQuery(id+"F8.imprint","IMPRINT",EDGE,{"derivedFrom":subQ0}),-1.0]])]});}
            var Q13;
            {var subQ0=sQuery(id+"F8.wireOp",EDGE,"E404.MirrorCS");Q13=makeQuery(id+"F8.imprint","IMPRINT",FACE,{"disambiguationData":[TD([[makeQuery(id+"F8.imprint","IMPRINT",EDGE,{"derivedFrom":subQ0}),-1.0]])]});}
            var Q14;
            {var subQ4=sQuery(id+"F8.wireOp",EDGE,"E407.MirrorCS");Q14=makeQuery(id+"F8.imprint","IMPRINT",FACE,{"disambiguationData":[TD([[makeQuery(id+"F8.imprint","IMPRINT",EDGE,{"derivedFrom":subQ4}),-1.0]])]});}
            extrude(context, id + "F9", {"entities" : qUnion([Q0, Q1, Q2, Q3, Q4, Q5, Q6, Q7, Q8, Q9, Q10, Q11, Q12, Q13, Q14]), "oppositeDirection" : true, "depth" : 4 * mm});
        }
    });
